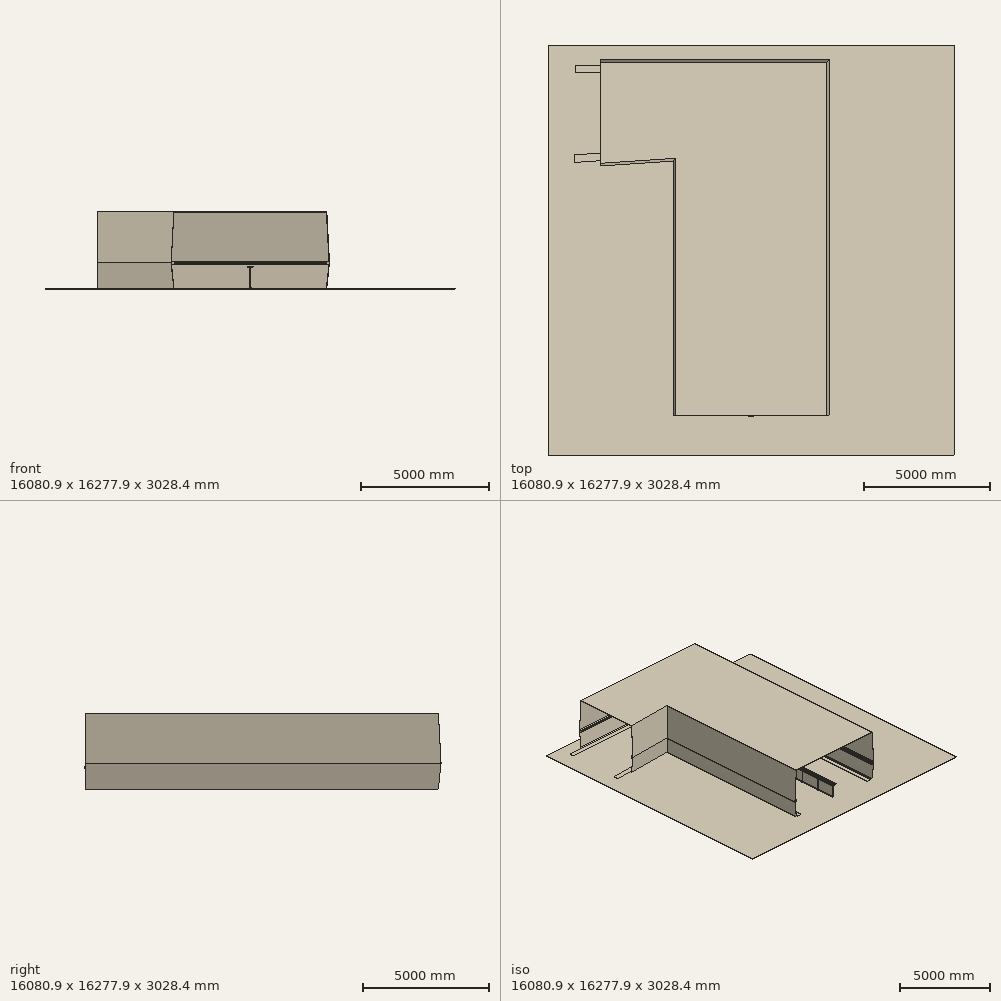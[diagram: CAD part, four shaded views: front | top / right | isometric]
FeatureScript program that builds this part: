
annotation { "Feature Type Name" : "Feature", "Feature Type Description" : "" }
export const myFeature = defineFeature(function(context is Context, id is Id, definition is map)
    precondition{}
    {
        {
            var Q0;
            Q0=qCreatedBy(makeId("Front.planeOp"),FACE);
            var sketch = newSketch(context, id + "F0", { "sketchPlane" : qUnion([Q0])});
            skLineSegment(sketch, "E0", {"start": v(-3000, -1500) * mm, "end": v(-3000, 1500) * mm, "construction": true});
            skLineSegment(sketch, "E1", {"start": v(-3000, 1500) * mm, "end": v(3000, 1500) * mm, "construction": true});
            skLineSegment(sketch, "E2", {"start": v(3000, 1500) * mm, "end": v(3000, -1500) * mm, "construction": true});
            skLineSegment(sketch, "E3.0", {"start": v(3000, 1504.6) * mm, "end": v(3000, -1500.4) * mm, "construction": true});
            skLineSegment(sketch, "E3.2", {"start": v(-3000, -1500.26) * mm, "end": v(-3000, 1504.6) * mm, "construction": true});
            skLineSegment(sketch, "E4", {"start": v(3000, 1504.6) * mm, "end": v(3104.82, -495.4) * mm});
            skLineSegment(sketch, "E5", {"start": v(3104.82, -495.4) * mm, "end": v(3000.17, -1498.75) * mm});
            skLineSegment(sketch, "E6.MirrorCS", {"start": v(-3000, 1504.6) * mm, "end": v(-3104.82, -495.4) * mm});
            skLineSegment(sketch, "E7.MirrorCS", {"start": v(-3104.82, -495.4) * mm, "end": v(-3000.17, -1498.75) * mm});
            skLineSegment(sketch, "E8", {"start": v(-3000, 1504.6) * mm, "end": v(3000, 1504.6) * mm});
            skLineSegment(sketch, "E9.0", {"start": v(3099.8, -495.26) * mm, "end": v(2995.14, -1498.75) * mm});
            skLineSegment(sketch, "E9.1", {"start": v(-3099.8, -495.26) * mm, "end": v(-2995.14, -1498.75) * mm});
            skLineSegment(sketch, "E9.2", {"start": v(-2995.26, 1499.6) * mm, "end": v(-3099.8, -495.26) * mm});
            skLineSegment(sketch, "E9.3", {"start": v(-2995.26, 1499.6) * mm, "end": v(2995.26, 1499.6) * mm});
            skLineSegment(sketch, "E9.4", {"start": v(2995.26, 1499.6) * mm, "end": v(3099.8, -495.26) * mm});
            skLineSegment(sketch, "E10", {"start": v(3000.17, -1498.75) * mm, "end": v(2995.14, -1498.75) * mm});
            skPoint(sketch, "E11.orphan", {"position": v(-3000, -1500.4) * mm});
            skLineSegment(sketch, "E12.trimOffspring", {"start": v(-2995.14, -1498.75) * mm, "end": v(-3000.17, -1498.75) * mm});
            skSolve(sketch);
        }
        {
            var Q0;
            Q0 = qSketchRegion(id + "F0", true);
            extrude(context, id + "F1", {"entities" : qUnion([Q0]), "oppositeDirection" : true, "depth" : 10000 * mm, "offsetDistance" : 25 * mm});
        }
        {
            var Q0;
            Q0=makeQuery(id+"F1.opExtrude","SWEPT_FACE",FACE,{"disambiguationData":[OSD([sQuery(id+"F0.wireOp",EDGE,"E12.trimOffspring")])]});
            var sketch = newSketch(context, id + "F2", { "sketchPlane" : qUnion([Q0])});
            skLineSegment(sketch, "E13.bottom", {"start": v(-8032.33, 1597.7) * mm, "end": v(8048.56, 1597.7) * mm});
            skLineSegment(sketch, "E13.top", {"start": v(-8032.33, -14680.18) * mm, "end": v(8048.56, -14680.18) * mm});
            skLineSegment(sketch, "E13.left", {"start": v(-8032.33, 1597.7) * mm, "end": v(-8032.33, -14680.18) * mm});
            skLineSegment(sketch, "E13.right", {"start": v(8048.56, 1597.7) * mm, "end": v(8048.56, -14680.18) * mm});
            skSolve(sketch);
        }
        {
            var Q0;
            Q0 = qSketchRegion(id + "F2", true);
            extrude(context, id + "F3", {"entities" : qUnion([Q0]), "depth" : 25 * mm, "offsetDistance" : 25 * mm});
        }
        {
            var Q0;
            Q0=makeQuery(id+"F1.opExtrude","CAP_FACE",FACE,{"disambiguationData":[OSD([sQuery(id+"F0.wireOp",EDGE,"E4"),sQuery(id+"F0.wireOp",EDGE,"E5"),sQuery(id+"F0.wireOp",EDGE,"E6.MirrorCS"),sQuery(id+"F0.wireOp",EDGE,"E7.MirrorCS"),sQuery(id+"F0.wireOp",EDGE,"E8"),sQuery(id+"F0.wireOp",EDGE,"E9.0"),sQuery(id+"F0.wireOp",EDGE,"E9.1"),sQuery(id+"F0.wireOp",EDGE,"E9.2"),sQuery(id+"F0.wireOp",EDGE,"E9.3"),sQuery(id+"F0.wireOp",EDGE,"E9.4"),sQuery(id+"F0.wireOp",EDGE,"E10"),sQuery(id+"F0.wireOp",EDGE,"E12.trimOffspring")])],"isStart":false});
            var sketch = newSketch(context, id + "F4", { "sketchPlane" : qUnion([Q0])});
            skLineSegment(sketch, "E14.0", {"start": v(-3000, 1504.6) * mm, "end": v(-3104.82, -495.4) * mm});
            skLineSegment(sketch, "E14.1", {"start": v(-2995.26, 1499.6) * mm, "end": v(-3099.8, -495.26) * mm});
            skLineSegment(sketch, "E14.2", {"start": v(-3099.8, -495.26) * mm, "end": v(-2995.14, -1498.75) * mm});
            skLineSegment(sketch, "E14.3", {"start": v(-3104.82, -495.4) * mm, "end": v(-3000.17, -1498.75) * mm});
            skLineSegment(sketch, "E14.4", {"start": v(-3000.17, -1498.75) * mm, "end": v(-2995.14, -1498.75) * mm});
            skLineSegment(sketch, "E15", {"start": v(-2995.26, 1499.6) * mm, "end": v(-2995.26, 1504.6) * mm});
            skLineSegment(sketch, "E16", {"start": v(-2995.26, 1504.6) * mm, "end": v(-3000, 1504.6) * mm});
            skSolve(sketch);
        }
        {
            var Q0;
            Q0=makeQuery(id+"F3.opExtrude","CAP_FACE",FACE,{"disambiguationData":[OSD([sQuery(id+"F2.wireOp",EDGE,"E13.bottom"),sQuery(id+"F2.wireOp",EDGE,"E13.top"),sQuery(id+"F2.wireOp",EDGE,"E13.left"),sQuery(id+"F2.wireOp",EDGE,"E13.right")])],"isStart":true});
            var sketch = newSketch(context, id + "F5", { "sketchPlane" : qUnion([Q0])});
            skLineSegment(sketch, "E17", {"start": v(3000.17, 10000) * mm, "end": v(3000.17, 14000) * mm});
            skLineSegment(sketch, "E18", {"start": v(3000.17, 14000) * mm, "end": v(-5999.83, 14000) * mm});
            skSolve(sketch);
        }
        {
            var Q0;
            Q0 = qSketchRegion(id + "F4", true);
            var Q1;
            Q1 = qConstructionFilter(qBodyType(qCreatedBy(id + "F5" ,EDGE), BodyType.WIRE), ConstructionObject.NO);
            sweep(context, id + "F6", {"operationType" : NewBodyOperationType.ADD, "profiles" : qUnion([Q0]), "path" : qUnion([Q1])});
        }
        {
            var Q0;
            Q0=makeQuery(id+"F1.opExtrude","CAP_FACE",FACE,{"disambiguationData":[OSD([sQuery(id+"F0.wireOp",EDGE,"E4"),sQuery(id+"F0.wireOp",EDGE,"E5"),sQuery(id+"F0.wireOp",EDGE,"E6.MirrorCS"),sQuery(id+"F0.wireOp",EDGE,"E7.MirrorCS"),sQuery(id+"F0.wireOp",EDGE,"E8"),sQuery(id+"F0.wireOp",EDGE,"E9.0"),sQuery(id+"F0.wireOp",EDGE,"E9.1"),sQuery(id+"F0.wireOp",EDGE,"E9.2"),sQuery(id+"F0.wireOp",EDGE,"E9.3"),sQuery(id+"F0.wireOp",EDGE,"E9.4"),sQuery(id+"F0.wireOp",EDGE,"E10"),sQuery(id+"F0.wireOp",EDGE,"E12.trimOffspring")])],"isStart":false});
            var sketch = newSketch(context, id + "F7", { "sketchPlane" : qUnion([Q0])});
            skLineSegment(sketch, "E19.0", {"start": v(3099.8, -495.26) * mm, "end": v(2995.14, -1498.75) * mm});
            skLineSegment(sketch, "E19.1", {"start": v(3104.82, -495.4) * mm, "end": v(3000.17, -1498.75) * mm});
            skLineSegment(sketch, "E19.2", {"start": v(2995.14, -1498.75) * mm, "end": v(3000.17, -1498.75) * mm});
            skLineSegment(sketch, "E19.3", {"start": v(3000, 1504.6) * mm, "end": v(3104.82, -495.4) * mm});
            skLineSegment(sketch, "E19.4", {"start": v(2995.26, 1499.6) * mm, "end": v(3099.8, -495.26) * mm});
            skLineSegment(sketch, "E20", {"start": v(2995.26, 1499.6) * mm, "end": v(2995.26, 1504.6) * mm});
            skLineSegment(sketch, "E21", {"start": v(2995.26, 1504.6) * mm, "end": v(3000, 1504.6) * mm});
            skSolve(sketch);
        }
        {
            var Q0;
            Q0=makeQuery(id+"F3.opExtrude","CAP_FACE",FACE,{"disambiguationData":[OSD([sQuery(id+"F2.wireOp",EDGE,"E13.bottom"),sQuery(id+"F2.wireOp",EDGE,"E13.top"),sQuery(id+"F2.wireOp",EDGE,"E13.left"),sQuery(id+"F2.wireOp",EDGE,"E13.right")])],"isStart":true});
            var sketch = newSketch(context, id + "F8", { "sketchPlane" : qUnion([Q0])});
            skLineSegment(sketch, "E22", {"start": v(-3000.17, 10000) * mm, "end": v(-3000.17, 10200) * mm});
            skLineSegment(sketch, "E23", {"start": v(-3000.17, 10200) * mm, "end": v(-5999.83, 10000) * mm});
            skSolve(sketch);
        }
        {
            var Q0;
            Q0 = qSketchRegion(id + "F7", true);
            var Q1;
            Q1 = qConstructionFilter(qBodyType(qCreatedBy(id + "F8" ,EDGE), BodyType.WIRE), ConstructionObject.NO);
            sweep(context, id + "F9", {"operationType" : NewBodyOperationType.ADD, "profiles" : qUnion([Q0]), "path" : qUnion([Q1])});
        }
        {
            var Q0;
            Q0=makeQuery(id+"F9.boolean.opBoolean","MERGE",FACE,{"derivedFrom":[makeQuery(id+"F6.boolean.opBoolean","MERGE",FACE,{"derivedFrom":[makeQuery(id+"F1.opExtrude","SWEPT_FACE",FACE,{"disambiguationData":[OSD([sQuery(id+"F0.wireOp",EDGE,"E8")])]}),makeQuery(id+"F6.opSweep","SWEPT_FACE",FACE,{"disambiguationData":[OSD([sQuery(id+"F4.wireOp",EDGE,"E16"),sQuery(id+"F5.wireOp",EDGE,"E17")])]})]}),makeQuery(id+"F9.opSweep","SWEPT_FACE",FACE,{"disambiguationData":[OSD([sQuery(id+"F7.wireOp",EDGE,"E21"),sQuery(id+"F8.wireOp",EDGE,"E22")])]})]});
            var sketch = newSketch(context, id + "F10", { "sketchPlane" : qUnion([Q0])});
            skLineSegment(sketch, "E24.0", {"start": v(-3000, 10200.18) * mm, "end": v(-5999.84, 10000.17) * mm});
            skLineSegment(sketch, "E24.1", {"start": v(3000, 13999.83) * mm, "end": v(-5999.83, 13999.83) * mm});
            skLineSegment(sketch, "E24.2", {"start": v(3000, 13999.83) * mm, "end": v(3000, 10000) * mm});
            skLineSegment(sketch, "E24.3", {"start": v(-2995.26, 10000) * mm, "end": v(2995.26, 10000) * mm});
            skLineSegment(sketch, "E25", {"start": v(2995.26, 10000) * mm, "end": v(3000, 10000) * mm});
            skPoint(sketch, "E26.orphan", {"position": v(3000, 0) * mm});
            skLineSegment(sketch, "E27", {"start": v(-3000, 10200.18) * mm, "end": v(-3000, 10000) * mm});
            skLineSegment(sketch, "E28", {"start": v(-3000, 10000) * mm, "end": v(-2995.26, 10000) * mm});
            skLineSegment(sketch, "E29", {"start": v(-5999.83, 13999.83) * mm, "end": v(-5999.84, 10000.17) * mm});
            skSolve(sketch);
        }
        {
            var Q0;
            Q0 = qSketchRegion(id + "F10", true);
            extrude(context, id + "F11", {"entities" : qUnion([Q0]), "operationType" : NewBodyOperationType.ADD, "oppositeDirection" : true, "depth" : 5 * mm, "offsetDistance" : 25 * mm});
        }
        {
            var Q0;
            Q0=makeQuery(id+"F1.opExtrude","CAP_FACE",FACE,{"disambiguationData":[OSD([sQuery(id+"F0.wireOp",EDGE,"E4"),sQuery(id+"F0.wireOp",EDGE,"E5"),sQuery(id+"F0.wireOp",EDGE,"E6.MirrorCS"),sQuery(id+"F0.wireOp",EDGE,"E7.MirrorCS"),sQuery(id+"F0.wireOp",EDGE,"E8"),sQuery(id+"F0.wireOp",EDGE,"E9.0"),sQuery(id+"F0.wireOp",EDGE,"E9.1"),sQuery(id+"F0.wireOp",EDGE,"E9.2"),sQuery(id+"F0.wireOp",EDGE,"E9.3"),sQuery(id+"F0.wireOp",EDGE,"E9.4"),sQuery(id+"F0.wireOp",EDGE,"E10"),sQuery(id+"F0.wireOp",EDGE,"E12.trimOffspring")])],"isStart":true});
            var sketch = newSketch(context, id + "F12", { "sketchPlane" : qUnion([Q0])});
            skLineSegment(sketch, "E30", {"start": v(3096.13, -425.26) * mm, "end": v(2976.13, -425.26) * mm});
            skLineSegment(sketch, "E31", {"start": v(2976.13, -425.26) * mm, "end": v(2976.13, -465.26) * mm});
            skLineSegment(sketch, "E32", {"start": v(2976.13, -565.26) * mm, "end": v(3016.19, -565.26) * mm});
            skLineSegment(sketch, "E33", {"start": v(3092.5, -565.26) * mm, "end": v(3099.8, -495.26) * mm});
            skLineSegment(sketch, "E34", {"start": v(3099.8, -495.26) * mm, "end": v(3096.13, -425.26) * mm});
            skLineSegment(sketch, "E35", {"start": v(2976.13, -525.26) * mm, "end": v(2986.13, -525.26) * mm});
            skLineSegment(sketch, "E36", {"start": v(2986.13, -525.26) * mm, "end": v(2986.13, -515.26) * mm});
            skLineSegment(sketch, "E37", {"start": v(2986.13, -515.26) * mm, "end": v(2976.13, -515.26) * mm});
            skLineSegment(sketch, "E38", {"start": v(2976.13, -465.26) * mm, "end": v(2986.13, -465.26) * mm});
            skLineSegment(sketch, "E39", {"start": v(2986.13, -465.26) * mm, "end": v(2986.13, -475.26) * mm});
            skLineSegment(sketch, "E40", {"start": v(2986.13, -475.26) * mm, "end": v(2976.13, -475.26) * mm});
            skLineSegment(sketch, "E41.trimOffspring", {"start": v(2976.13, -475.26) * mm, "end": v(2976.13, -515.26) * mm});
            skLineSegment(sketch, "E42.trimOffspring", {"start": v(2976.13, -525.26) * mm, "end": v(2976.13, -565.26) * mm});
            skLineSegment(sketch, "E43", {"start": v(3034.32, -565.26) * mm, "end": v(3034.32, -541.62) * mm, "construction": true});
            skLineSegment(sketch, "E44", {"start": v(3034.32, -541.62) * mm, "end": v(3024.32, -541.62) * mm});
            skLineSegment(sketch, "E45", {"start": v(3024.32, -541.62) * mm, "end": v(3016.19, -565.26) * mm});
            skLineSegment(sketch, "E46.MirrorCS", {"start": v(3044.32, -541.62) * mm, "end": v(3052.45, -565.26) * mm});
            skLineSegment(sketch, "E47.MirrorCS", {"start": v(3034.32, -541.62) * mm, "end": v(3044.32, -541.62) * mm});
            skLineSegment(sketch, "E48.trimOffspring", {"start": v(3052.45, -565.26) * mm, "end": v(3092.5, -565.26) * mm});
            skSolve(sketch);
        }
        {
            var Q0;
            Q0 = qSketchRegion(id + "F12", true);
            var Q1;
            Q1=makeQuery(id+"F6.boolean.opBoolean","MERGE",EDGE,{"derivedFrom":[makeQuery(id+"F1.opExtrude","SWEPT_EDGE",EDGE,{"disambiguationData":[OSD([sQuery(id+"F0.wireOp",EDGE,"E9.0"),sQuery(id+"F0.wireOp",EDGE,"E9.4")])]}),makeQuery(id+"F6.opSweep","SWEPT_EDGE",EDGE,{"disambiguationData":[OSD([sQuery(id+"F4.wireOp",EDGE,"E14.1"),sQuery(id+"F4.wireOp",EDGE,"E14.2"),sQuery(id+"F5.wireOp",EDGE,"E17")])]})]});
            var Q2;
            Q2=makeQuery(id+"F6.opSweep","SWEPT_EDGE",EDGE,{"disambiguationData":[OSD([sQuery(id+"F4.wireOp",EDGE,"E14.1"),sQuery(id+"F4.wireOp",EDGE,"E14.2"),sQuery(id+"F5.wireOp",EDGE,"E18")])]});
            sweep(context, id + "F13", {"profiles" : qUnion([Q0]), "path" : qUnion([Q1, Q2])});
        }
        {
            var Q0;
            {var subQ0=sQuery(id+"F0.wireOp",EDGE,"E9.4");var subQ1=sQuery(id+"F0.wireOp",EDGE,"E9.0");Q0=makeQuery(id+"F13.boolean.opBoolean","MERGE",FACE,{"derivedFrom":[makeQuery(id+"F1.opExtrude","CAP_FACE",FACE,{"disambiguationData":[OSD([sQuery(id+"F0.wireOp",EDGE,"E4"),sQuery(id+"F0.wireOp",EDGE,"E5"),sQuery(id+"F0.wireOp",EDGE,"E6.MirrorCS"),sQuery(id+"F0.wireOp",EDGE,"E7.MirrorCS"),sQuery(id+"F0.wireOp",EDGE,"E8"),subQ1,sQuery(id+"F0.wireOp",EDGE,"E9.1"),sQuery(id+"F0.wireOp",EDGE,"E9.2"),sQuery(id+"F0.wireOp",EDGE,"E9.3"),subQ0,sQuery(id+"F0.wireOp",EDGE,"E10"),sQuery(id+"F0.wireOp",EDGE,"E12.trimOffspring")])],"isStart":true}),makeQuery(id+"F13.opSweep","CAP_FACE",FACE,{"disambiguationData":[OSD([subQ1,subQ0,sQuery(id+"F12.wireOp",EDGE,"E30"),sQuery(id+"F12.wireOp",EDGE,"E31"),sQuery(id+"F12.wireOp",EDGE,"E32"),sQuery(id+"F12.wireOp",EDGE,"E33"),sQuery(id+"F12.wireOp",EDGE,"E34"),sQuery(id+"F12.wireOp",EDGE,"E35"),sQuery(id+"F12.wireOp",EDGE,"E36"),sQuery(id+"F12.wireOp",EDGE,"E37"),sQuery(id+"F12.wireOp",EDGE,"E38"),sQuery(id+"F12.wireOp",EDGE,"E39"),sQuery(id+"F12.wireOp",EDGE,"E40"),sQuery(id+"F12.wireOp",EDGE,"E41.trimOffspring"),sQuery(id+"F12.wireOp",EDGE,"E42.trimOffspring"),sQuery(id+"F12.wireOp",EDGE,"E44"),sQuery(id+"F12.wireOp",EDGE,"E45"),sQuery(id+"F12.wireOp",EDGE,"E46.MirrorCS"),sQuery(id+"F12.wireOp",EDGE,"E47.MirrorCS"),sQuery(id+"F12.wireOp",EDGE,"E48.trimOffspring")])],"isStart":true})]});}
            var sketch = newSketch(context, id + "F14", { "sketchPlane" : qUnion([Q0])});
            skLineSegment(sketch, "E49.0", {"start": v(3096.13, -425.26) * mm, "end": v(2976.13, -425.26) * mm, "construction": true});
            skLineSegment(sketch, "E49.1", {"start": v(2976.13, -425.26) * mm, "end": v(2976.13, -465.26) * mm, "construction": true});
            skLineSegment(sketch, "E49.2", {"start": v(2976.13, -565.26) * mm, "end": v(3016.19, -565.26) * mm, "construction": true});
            skLineSegment(sketch, "E49.3", {"start": v(3092.5, -565.26) * mm, "end": v(3099.8, -495.26) * mm, "construction": true});
            skLineSegment(sketch, "E49.4", {"start": v(3099.8, -495.26) * mm, "end": v(3096.13, -425.26) * mm, "construction": true});
            skLineSegment(sketch, "E49.5", {"start": v(2976.13, -525.26) * mm, "end": v(2986.13, -525.26) * mm, "construction": true});
            skLineSegment(sketch, "E49.6", {"start": v(2986.13, -525.26) * mm, "end": v(2986.13, -515.26) * mm, "construction": true});
            skLineSegment(sketch, "E49.7", {"start": v(2986.13, -515.26) * mm, "end": v(2976.13, -515.26) * mm, "construction": true});
            skLineSegment(sketch, "E49.8", {"start": v(2976.13, -465.26) * mm, "end": v(2986.13, -465.26) * mm, "construction": true});
            skLineSegment(sketch, "E49.9", {"start": v(2986.13, -465.26) * mm, "end": v(2986.13, -475.26) * mm, "construction": true});
            skLineSegment(sketch, "E49.10", {"start": v(2986.13, -475.26) * mm, "end": v(2976.13, -475.26) * mm, "construction": true});
            skLineSegment(sketch, "E49.11", {"start": v(2976.13, -475.26) * mm, "end": v(2976.13, -515.26) * mm, "construction": true});
            skLineSegment(sketch, "E49.12", {"start": v(2976.13, -525.26) * mm, "end": v(2976.13, -565.26) * mm, "construction": true});
            skLineSegment(sketch, "E49.13", {"start": v(3034.32, -565.26) * mm, "end": v(3034.32, -541.62) * mm, "construction": true});
            skLineSegment(sketch, "E49.14", {"start": v(3034.32, -541.62) * mm, "end": v(3024.32, -541.62) * mm, "construction": true});
            skLineSegment(sketch, "E49.15", {"start": v(3024.32, -541.62) * mm, "end": v(3016.19, -565.26) * mm, "construction": true});
            skLineSegment(sketch, "E49.16", {"start": v(3044.32, -541.62) * mm, "end": v(3052.45, -565.26) * mm, "construction": true});
            skLineSegment(sketch, "E49.17", {"start": v(3034.32, -541.62) * mm, "end": v(3044.32, -541.62) * mm, "construction": true});
            skLineSegment(sketch, "E49.18", {"start": v(3052.45, -565.26) * mm, "end": v(3092.5, -565.26) * mm, "construction": true});
            skLineSegment(sketch, "E50", {"start": v(3099.8, -495.26) * mm, "end": v(-3099.8, -495.26) * mm, "construction": true});
            skLineSegment(sketch, "E51", {"start": v(0, -495.26) * mm, "end": v(0, -210.15) * mm, "construction": true});
            skLineSegment(sketch, "E52.MirrorCS", {"start": v(-2976.13, -525.26) * mm, "end": v(-2976.13, -565.26) * mm});
            skLineSegment(sketch, "E53.MirrorCS", {"start": v(-2976.13, -475.26) * mm, "end": v(-2976.13, -515.26) * mm});
            skLineSegment(sketch, "E54.MirrorCS", {"start": v(-2986.13, -475.26) * mm, "end": v(-2976.13, -475.26) * mm});
            skLineSegment(sketch, "E55.MirrorCS", {"start": v(-2986.13, -465.26) * mm, "end": v(-2986.13, -475.26) * mm});
            skLineSegment(sketch, "E56.MirrorCS", {"start": v(-2976.13, -465.26) * mm, "end": v(-2986.13, -465.26) * mm});
            skLineSegment(sketch, "E57.MirrorCS", {"start": v(-2986.13, -515.26) * mm, "end": v(-2976.13, -515.26) * mm});
            skLineSegment(sketch, "E58.MirrorCS", {"start": v(-3044.32, -541.62) * mm, "end": v(-3052.45, -565.26) * mm});
            skLineSegment(sketch, "E59.MirrorCS", {"start": v(-2986.13, -525.26) * mm, "end": v(-2986.13, -515.26) * mm});
            skLineSegment(sketch, "E60.MirrorCS", {"start": v(-2976.13, -525.26) * mm, "end": v(-2986.13, -525.26) * mm});
            skLineSegment(sketch, "E61.MirrorCS", {"start": v(-3052.45, -565.26) * mm, "end": v(-3092.5, -565.26) * mm});
            skLineSegment(sketch, "E62.MirrorCS", {"start": v(-3099.8, -495.26) * mm, "end": v(-3096.13, -425.26) * mm});
            skLineSegment(sketch, "E63.MirrorCS", {"start": v(-3092.5, -565.26) * mm, "end": v(-3099.8, -495.26) * mm});
            skLineSegment(sketch, "E64.MirrorCS", {"start": v(-2976.13, -565.26) * mm, "end": v(-3016.19, -565.26) * mm});
            skLineSegment(sketch, "E65.MirrorCS", {"start": v(-2976.13, -425.26) * mm, "end": v(-2976.13, -465.26) * mm});
            skLineSegment(sketch, "E66.MirrorCS", {"start": v(-3096.13, -425.26) * mm, "end": v(-2976.13, -425.26) * mm});
            skLineSegment(sketch, "E67.MirrorCS", {"start": v(-3024.32, -541.62) * mm, "end": v(-3016.19, -565.26) * mm});
            skLineSegment(sketch, "E68.MirrorCS", {"start": v(-3034.32, -541.62) * mm, "end": v(-3024.32, -541.62) * mm});
            skLineSegment(sketch, "E69.MirrorCS", {"start": v(-3034.32, -541.62) * mm, "end": v(-3044.32, -541.62) * mm});
            skLineSegment(sketch, "E70.MirrorCS", {"start": v(-3034.32, -565.26) * mm, "end": v(-3034.32, -541.62) * mm});
            skSolve(sketch);
        }
        {
            var Q0;
            Q0 = qSketchRegion(id + "F14", true);
            var Q1;
            Q1=makeQuery(id+"F9.boolean.opBoolean","MERGE",EDGE,{"derivedFrom":[makeQuery(id+"F1.opExtrude","SWEPT_EDGE",EDGE,{"disambiguationData":[OSD([sQuery(id+"F0.wireOp",EDGE,"E9.1"),sQuery(id+"F0.wireOp",EDGE,"E9.2")])]}),makeQuery(id+"F9.opSweep","SWEPT_EDGE",EDGE,{"disambiguationData":[OSD([sQuery(id+"F7.wireOp",EDGE,"E19.0"),sQuery(id+"F7.wireOp",EDGE,"E19.4"),sQuery(id+"F8.wireOp",EDGE,"E22")])]})]});
            var Q2;
            Q2=makeQuery(id+"F9.opSweep","SWEPT_EDGE",EDGE,{"disambiguationData":[OSD([sQuery(id+"F7.wireOp",EDGE,"E19.0"),sQuery(id+"F7.wireOp",EDGE,"E19.4"),sQuery(id+"F8.wireOp",EDGE,"E23")])]});
            sweep(context, id + "F15", {"profiles" : qUnion([Q0]), "path" : qUnion([Q1, Q2])});
        }
        {
            var Q0;
            Q0=makeQuery(id+"F3.opExtrude","CAP_FACE",FACE,{"disambiguationData":[OSD([sQuery(id+"F2.wireOp",EDGE,"E13.bottom"),sQuery(id+"F2.wireOp",EDGE,"E13.top"),sQuery(id+"F2.wireOp",EDGE,"E13.left"),sQuery(id+"F2.wireOp",EDGE,"E13.right")])],"isStart":true});
            var sketch = newSketch(context, id + "F16", { "sketchPlane" : qUnion([Q0])});
            skLineSegment(sketch, "E71.0", {"start": v(-2895.14, 10312.26) * mm, "end": v(-2895.14, 0) * mm});
            skLineSegment(sketch, "E71.1", {"start": v(-2895.14, 10312.26) * mm, "end": v(-7004.33, 10038.29) * mm});
            skLineSegment(sketch, "E72.0", {"start": v(-2595.14, 10632.93) * mm, "end": v(-7016.35, 10338.15) * mm});
            skLineSegment(sketch, "E72.1", {"start": v(-2595.14, 10632.93) * mm, "end": v(-2595.14, 0) * mm});
            skLineSegment(sketch, "E73", {"start": v(-2895.14, 0) * mm, "end": v(-2595.14, 0) * mm});
            skLineSegment(sketch, "E74", {"start": v(-7016.35, 10338.15) * mm, "end": v(-7004.33, 10038.29) * mm});
            skLineSegment(sketch, "E75.0", {"start": v(2895.14, 13894.97) * mm, "end": v(2895.14, 0) * mm});
            skLineSegment(sketch, "E75.1", {"start": v(2895.14, 13894.97) * mm, "end": v(-6994.83, 13894.97) * mm});
            skLineSegment(sketch, "E76.0", {"start": v(2595.14, 13594.97) * mm, "end": v(2595.14, 0) * mm});
            skLineSegment(sketch, "E76.1", {"start": v(2595.14, 13594.97) * mm, "end": v(-6994.83, 13594.97) * mm});
            skLineSegment(sketch, "E77", {"start": v(2595.14, 0) * mm, "end": v(2895.14, 0) * mm});
            skLineSegment(sketch, "E78", {"start": v(-6994.83, 13594.97) * mm, "end": v(-6994.83, 13894.97) * mm});
            skSolve(sketch);
        }
        {
            var Q0;
            Q0 = qSketchRegion(id + "F16", true);
            extrude(context, id + "F17", {"entities" : qUnion([Q0]), "operationType" : NewBodyOperationType.REMOVE, "oppositeDirection" : true, "depth" : 25 * mm, "offsetDistance" : 25 * mm});
        }
        {
            var Q0;
            Q0=makeQuery(id+"F3.opExtrude","CAP_FACE",FACE,{"disambiguationData":[OSD([sQuery(id+"F2.wireOp",EDGE,"E13.bottom"),sQuery(id+"F2.wireOp",EDGE,"E13.top"),sQuery(id+"F2.wireOp",EDGE,"E13.left"),sQuery(id+"F2.wireOp",EDGE,"E13.right")])],"isStart":true});
            var sketch = newSketch(context, id + "F18", { "sketchPlane" : qUnion([Q0])});
            skLineSegment(sketch, "E79.0", {"start": v(-2895.14, 10312.26) * mm, "end": v(-2895.14, 0) * mm});
            skLineSegment(sketch, "E79.1", {"start": v(-2895.14, 0) * mm, "end": v(-2595.14, 0) * mm});
            skLineSegment(sketch, "E79.2", {"start": v(-2595.14, 10632.93) * mm, "end": v(-2595.14, 0) * mm});
            skLineSegment(sketch, "E79.3", {"start": v(2595.14, 13594.97) * mm, "end": v(2595.14, 0) * mm});
            skLineSegment(sketch, "E79.4", {"start": v(2595.14, 0) * mm, "end": v(2895.14, 0) * mm});
            skLineSegment(sketch, "E79.5", {"start": v(2895.14, 13894.97) * mm, "end": v(2895.14, 0) * mm});
            skLineSegment(sketch, "E79.6", {"start": v(-2595.14, 10632.93) * mm, "end": v(-7016.35, 10338.15) * mm});
            skLineSegment(sketch, "E79.7", {"start": v(-7016.35, 10338.15) * mm, "end": v(-7004.33, 10038.29) * mm});
            skLineSegment(sketch, "E79.8", {"start": v(-2895.14, 10312.26) * mm, "end": v(-7004.33, 10038.29) * mm});
            skLineSegment(sketch, "E79.9", {"start": v(2895.14, 13894.97) * mm, "end": v(-6994.83, 13894.97) * mm});
            skLineSegment(sketch, "E79.10", {"start": v(2595.14, 13594.97) * mm, "end": v(-6994.83, 13594.97) * mm});
            skLineSegment(sketch, "E79.11", {"start": v(-6994.83, 13594.97) * mm, "end": v(-6994.83, 13894.97) * mm});
            skPoint(sketch, "E79.12", {"position": v(2745.14, 0) * mm});
            skSolve(sketch);
        }
        {
            var Q0;
            Q0 = qSketchRegion(id + "F18", true);
            var Q1;
            Q1=makeQuery(id+"F3.opExtrude","CAP_FACE",FACE,{"disambiguationData":[OSD([sQuery(id+"F2.wireOp",EDGE,"E13.bottom"),sQuery(id+"F2.wireOp",EDGE,"E13.top"),sQuery(id+"F2.wireOp",EDGE,"E13.left"),sQuery(id+"F2.wireOp",EDGE,"E13.right")])],"isStart":false});
            extrude(context, id + "F19", {"entities" : qUnion([Q0]), "endBound" : BoundingType.UP_TO_SURFACE, "oppositeDirection" : true, "depth" : 25 * mm, "endBoundEntityFace" : qUnion([Q1]), "offsetDistance" : 25 * mm});
        }
        {
            var Q0;
            Q0=makeQuery(id+"F13.opSweep","MID_CAP_EDGE",EDGE,{"disambiguationData":[OSD([sQuery(id+"F4.wireOp",EDGE,"E14.1"),sQuery(id+"F4.wireOp",EDGE,"E14.2"),sQuery(id+"F5.wireOp",EDGE,"E17"),sQuery(id+"F12.wireOp",EDGE,"E31")])],"capPos":1.0});
            var Q1;
            Q1=makeQuery(id+"F13.opSweep","MID_CAP_EDGE",EDGE,{"disambiguationData":[OSD([sQuery(id+"F4.wireOp",EDGE,"E14.1"),sQuery(id+"F4.wireOp",EDGE,"E14.2"),sQuery(id+"F5.wireOp",EDGE,"E17"),sQuery(id+"F12.wireOp",EDGE,"E42.trimOffspring")])],"capPos":1.0});
            var Q2;
            Q2=makeQuery(id+"F13.opSweep","MID_CAP_EDGE",EDGE,{"disambiguationData":[OSD([sQuery(id+"F4.wireOp",EDGE,"E14.1"),sQuery(id+"F4.wireOp",EDGE,"E14.2"),sQuery(id+"F5.wireOp",EDGE,"E17"),sQuery(id+"F12.wireOp",EDGE,"E41.trimOffspring")])],"capPos":1.0});
            var Q3;
            Q3=makeQuery(id+"F15.opSweep","MID_CAP_EDGE",EDGE,{"disambiguationData":[OSD([sQuery(id+"F7.wireOp",EDGE,"E19.0"),sQuery(id+"F7.wireOp",EDGE,"E19.4"),sQuery(id+"F8.wireOp",EDGE,"E22"),sQuery(id+"F14.wireOp",EDGE,"E65.MirrorCS")])],"capPos":1.0});
            var Q4;
            Q4=makeQuery(id+"F15.opSweep","MID_CAP_EDGE",EDGE,{"disambiguationData":[OSD([sQuery(id+"F7.wireOp",EDGE,"E19.0"),sQuery(id+"F7.wireOp",EDGE,"E19.4"),sQuery(id+"F8.wireOp",EDGE,"E22"),sQuery(id+"F14.wireOp",EDGE,"E53.MirrorCS")])],"capPos":1.0});
            var Q5;
            Q5=makeQuery(id+"F15.opSweep","MID_CAP_EDGE",EDGE,{"disambiguationData":[OSD([sQuery(id+"F7.wireOp",EDGE,"E19.0"),sQuery(id+"F7.wireOp",EDGE,"E19.4"),sQuery(id+"F8.wireOp",EDGE,"E22"),sQuery(id+"F14.wireOp",EDGE,"E52.MirrorCS")])],"capPos":1.0});
            var Q6;
            Q6=makeQuery(id+"F15.opSweep","MID_CAP_EDGE",EDGE,{"disambiguationData":[OSD([sQuery(id+"F7.wireOp",EDGE,"E19.0"),sQuery(id+"F7.wireOp",EDGE,"E19.4"),sQuery(id+"F8.wireOp",EDGE,"E22"),sQuery(id+"F14.wireOp",EDGE,"E55.MirrorCS")])],"capPos":1.0});
            var Q7;
            Q7=makeQuery(id+"F15.opSweep","MID_CAP_EDGE",EDGE,{"disambiguationData":[OSD([sQuery(id+"F7.wireOp",EDGE,"E19.0"),sQuery(id+"F7.wireOp",EDGE,"E19.4"),sQuery(id+"F8.wireOp",EDGE,"E22"),sQuery(id+"F14.wireOp",EDGE,"E59.MirrorCS")])],"capPos":1.0});
            fillet(context, id + "F20", {"entities" : qUnion([Q0, Q1, Q2, Q3, Q4, Q5, Q6, Q7]), "radius" : 5 * mm, "tangentPropagation" : true, "allowEdgeOverflow" : false});
        }
        {
            var Q0;
            Q0=makeQuery(id+"F13.opSweep","SWEPT_EDGE",EDGE,{"disambiguationData":[OSD([sQuery(id+"F0.wireOp",EDGE,"E9.0"),sQuery(id+"F0.wireOp",EDGE,"E9.4"),sQuery(id+"F4.wireOp",EDGE,"E14.1"),sQuery(id+"F4.wireOp",EDGE,"E14.2"),sQuery(id+"F5.wireOp",EDGE,"E17"),sQuery(id+"F12.wireOp",EDGE,"E30"),sQuery(id+"F12.wireOp",EDGE,"E31")])]});
            var Q1;
            Q1=makeQuery(id+"F13.opSweep","SWEPT_EDGE",EDGE,{"disambiguationData":[OSD([sQuery(id+"F0.wireOp",EDGE,"E9.0"),sQuery(id+"F0.wireOp",EDGE,"E9.4"),sQuery(id+"F4.wireOp",EDGE,"E14.1"),sQuery(id+"F4.wireOp",EDGE,"E14.2"),sQuery(id+"F5.wireOp",EDGE,"E17"),sQuery(id+"F12.wireOp",EDGE,"E32"),sQuery(id+"F12.wireOp",EDGE,"E42.trimOffspring")])]});
            var Q2;
            Q2=makeQuery(id+"F15.opSweep","SWEPT_EDGE",EDGE,{"disambiguationData":[OSD([sQuery(id+"F0.wireOp",EDGE,"E9.1"),sQuery(id+"F0.wireOp",EDGE,"E9.2"),sQuery(id+"F7.wireOp",EDGE,"E19.0"),sQuery(id+"F7.wireOp",EDGE,"E19.4"),sQuery(id+"F8.wireOp",EDGE,"E22"),sQuery(id+"F14.wireOp",EDGE,"E65.MirrorCS"),sQuery(id+"F14.wireOp",EDGE,"E66.MirrorCS")])]});
            var Q3;
            Q3=makeQuery(id+"F15.opSweep","SWEPT_EDGE",EDGE,{"disambiguationData":[OSD([sQuery(id+"F0.wireOp",EDGE,"E9.1"),sQuery(id+"F0.wireOp",EDGE,"E9.2"),sQuery(id+"F7.wireOp",EDGE,"E19.0"),sQuery(id+"F7.wireOp",EDGE,"E19.4"),sQuery(id+"F8.wireOp",EDGE,"E22"),sQuery(id+"F14.wireOp",EDGE,"E52.MirrorCS"),sQuery(id+"F14.wireOp",EDGE,"E64.MirrorCS")])]});
            fillet(context, id + "F21", {"entities" : qUnion([Q0, Q1, Q2, Q3]), "radius" : 10 * mm, "tangentPropagation" : true, "allowEdgeOverflow" : false});
        }
        {
            var Q0;
            Q0=makeQuery(id+"F15.opSweep","SWEPT_EDGE",EDGE,{"disambiguationData":[OSD([sQuery(id+"F7.wireOp",EDGE,"E19.0"),sQuery(id+"F7.wireOp",EDGE,"E19.4"),sQuery(id+"F8.wireOp",EDGE,"E23"),sQuery(id+"F14.wireOp",EDGE,"E56.MirrorCS"),sQuery(id+"F14.wireOp",EDGE,"E65.MirrorCS")])]});
            var Q1;
            Q1=makeQuery(id+"F15.opSweep","SWEPT_EDGE",EDGE,{"disambiguationData":[OSD([sQuery(id+"F7.wireOp",EDGE,"E19.0"),sQuery(id+"F7.wireOp",EDGE,"E19.4"),sQuery(id+"F8.wireOp",EDGE,"E23"),sQuery(id+"F14.wireOp",EDGE,"E53.MirrorCS"),sQuery(id+"F14.wireOp",EDGE,"E54.MirrorCS")])]});
            var Q2;
            Q2=makeQuery(id+"F15.opSweep","SWEPT_EDGE",EDGE,{"disambiguationData":[OSD([sQuery(id+"F7.wireOp",EDGE,"E19.0"),sQuery(id+"F7.wireOp",EDGE,"E19.4"),sQuery(id+"F8.wireOp",EDGE,"E23"),sQuery(id+"F14.wireOp",EDGE,"E53.MirrorCS"),sQuery(id+"F14.wireOp",EDGE,"E57.MirrorCS")])]});
            var Q3;
            Q3=makeQuery(id+"F15.opSweep","SWEPT_EDGE",EDGE,{"disambiguationData":[OSD([sQuery(id+"F7.wireOp",EDGE,"E19.0"),sQuery(id+"F7.wireOp",EDGE,"E19.4"),sQuery(id+"F8.wireOp",EDGE,"E23"),sQuery(id+"F14.wireOp",EDGE,"E52.MirrorCS"),sQuery(id+"F14.wireOp",EDGE,"E60.MirrorCS")])]});
            var Q4;
            Q4=makeQuery(id+"F13.opSweep","SWEPT_EDGE",EDGE,{"disambiguationData":[OSD([sQuery(id+"F0.wireOp",EDGE,"E9.0"),sQuery(id+"F0.wireOp",EDGE,"E9.4"),sQuery(id+"F4.wireOp",EDGE,"E14.1"),sQuery(id+"F4.wireOp",EDGE,"E14.2"),sQuery(id+"F5.wireOp",EDGE,"E17"),sQuery(id+"F12.wireOp",EDGE,"E35"),sQuery(id+"F12.wireOp",EDGE,"E42.trimOffspring")])]});
            var Q5;
            Q5=makeQuery(id+"F13.opSweep","SWEPT_EDGE",EDGE,{"disambiguationData":[OSD([sQuery(id+"F0.wireOp",EDGE,"E9.0"),sQuery(id+"F0.wireOp",EDGE,"E9.4"),sQuery(id+"F4.wireOp",EDGE,"E14.1"),sQuery(id+"F4.wireOp",EDGE,"E14.2"),sQuery(id+"F5.wireOp",EDGE,"E17"),sQuery(id+"F12.wireOp",EDGE,"E37"),sQuery(id+"F12.wireOp",EDGE,"E41.trimOffspring")])]});
            var Q6;
            Q6=makeQuery(id+"F13.opSweep","SWEPT_EDGE",EDGE,{"disambiguationData":[OSD([sQuery(id+"F0.wireOp",EDGE,"E9.0"),sQuery(id+"F0.wireOp",EDGE,"E9.4"),sQuery(id+"F4.wireOp",EDGE,"E14.1"),sQuery(id+"F4.wireOp",EDGE,"E14.2"),sQuery(id+"F5.wireOp",EDGE,"E17"),sQuery(id+"F12.wireOp",EDGE,"E40"),sQuery(id+"F12.wireOp",EDGE,"E41.trimOffspring")])]});
            var Q7;
            Q7=makeQuery(id+"F13.opSweep","SWEPT_EDGE",EDGE,{"disambiguationData":[OSD([sQuery(id+"F0.wireOp",EDGE,"E9.0"),sQuery(id+"F0.wireOp",EDGE,"E9.4"),sQuery(id+"F4.wireOp",EDGE,"E14.1"),sQuery(id+"F4.wireOp",EDGE,"E14.2"),sQuery(id+"F5.wireOp",EDGE,"E17"),sQuery(id+"F12.wireOp",EDGE,"E31"),sQuery(id+"F12.wireOp",EDGE,"E38")])]});
            fillet(context, id + "F22", {"entities" : qUnion([Q0, Q1, Q2, Q3, Q4, Q5, Q6, Q7]), "radius" : 5 * mm, "tangentPropagation" : true, "allowEdgeOverflow" : false});
        }
        {
            var Q0;
            Q0=makeQuery(id+"F3.opExtrude","CAP_FACE",FACE,{"disambiguationData":[OSD([sQuery(id+"F2.wireOp",EDGE,"E13.bottom"),sQuery(id+"F2.wireOp",EDGE,"E13.top"),sQuery(id+"F2.wireOp",EDGE,"E13.left"),sQuery(id+"F2.wireOp",EDGE,"E13.right")])],"isStart":true});
            var sketch = newSketch(context, id + "F23", { "sketchPlane" : qUnion([Q0])});
            skLineSegment(sketch, "E80", {"start": v(-2595.14, 0) * mm, "end": v(2595.14, 0) * mm, "construction": true});
            skLineSegment(sketch, "E81", {"start": v(0, 0) * mm, "end": v(0, 10632.93) * mm, "construction": true});
            skCircle(sketch, "E82", {"center": v(0, 100) * mm, "radius": 40 * mm});
            skCircle(sketch, "E83.0.1.0", {"center": v(0, 1300) * mm, "radius": 40 * mm});
            skCircle(sketch, "E83.0.2.0", {"center": v(0, 2500) * mm, "radius": 40 * mm});
            skCircle(sketch, "E83.0.3.0", {"center": v(0, 3700) * mm, "radius": 40 * mm});
            skCircle(sketch, "E83.0.4.0", {"center": v(0, 4900) * mm, "radius": 40 * mm});
            skCircle(sketch, "E83.0.5.0", {"center": v(0, 6100) * mm, "radius": 40 * mm});
            skCircle(sketch, "E83.0.6.0", {"center": v(0, 7300) * mm, "radius": 40 * mm});
            skCircle(sketch, "E83.0.7.0", {"center": v(0, 8500) * mm, "radius": 40 * mm});
            skCircle(sketch, "E83.0.8.0", {"center": v(0, 9700) * mm, "radius": 40 * mm});
            skLineSegment(sketch, "E83.direction1", {"start": v(0, 100) * mm, "end": v(0, 100) * mm});
            skLineSegment(sketch, "E83.direction2", {"start": v(0, 100) * mm, "end": v(0, 1300) * mm, "construction": true});
            skSolve(sketch);
        }
        {
            var Q0;
            Q0 = qSketchRegion(id + "F23", true);
            extrude(context, id + "F24", {"entities" : qUnion([Q0]), "depth" : 25 * mm, "offsetDistance" : 25 * mm});
        }
        {
            var Q0;
            Q0=makeQuery(id+"F24.opExtrude","CAP_FACE",FACE,{"disambiguationData":[OSD([sQuery(id+"F23.wireOp",EDGE,"E82")])],"isStart":false});
            var sketch = newSketch(context, id + "F25", { "sketchPlane" : qUnion([Q0])});
            skArc(sketch, "E84", {"start": v(-6, 129.4) * mm, "mid": v(-11.18, 127.84) * mm, "end": v(-16, 125.38) * mm});
            skLineSegment(sketch, "E85", {"start": v(0, 100) * mm, "end": v(0, 130) * mm, "construction": true});
            skLineSegment(sketch, "E86.0", {"start": v(6, 100) * mm, "end": v(6, 129.4) * mm});
            skLineSegment(sketch, "E87.0", {"start": v(-6, 100) * mm, "end": v(-6, 129.4) * mm});
            skLineSegment(sketch, "E88", {"start": v(-6, 100) * mm, "end": v(6, 100) * mm});
            skCircle(sketch, "E89.0", {"center": v(0, 1300) * mm, "radius": 40 * mm, "construction": true});
            skArc(sketch, "E90", {"start": v(6, 1270.6) * mm, "mid": v(11.18, 1272.16) * mm, "end": v(16, 1274.62) * mm});
            skLineSegment(sketch, "E91.0", {"start": v(-6, 1292) * mm, "end": v(-6, 1270.6) * mm});
            skLineSegment(sketch, "E92.0", {"start": v(6, 1292) * mm, "end": v(6, 1270.6) * mm});
            skLineSegment(sketch, "E93", {"start": v(-6, 1292) * mm, "end": v(6, 1292) * mm});
            skPoint(sketch, "E93.endSnap0", {"position": v(6, 1285) * mm});
            skPoint(sketch, "E94.orphan", {"position": v(6, 1300) * mm});
            skPoint(sketch, "E95.orphan", {"position": v(6, 1270) * mm});
            skLineSegment(sketch, "E96", {"start": v(-20.78, 1300) * mm, "end": v(22.57, 1300) * mm, "construction": true});
            skLineSegment(sketch, "E97.MirrorCS", {"start": v(6, 1308) * mm, "end": v(6, 1329.4) * mm});
            skPoint(sketch, "E98.MirrorP", {"position": v(6, 1330) * mm});
            skPoint(sketch, "E99.MirrorP", {"position": v(6, 1315) * mm});
            skLineSegment(sketch, "E100.MirrorCS", {"start": v(-6, 1308) * mm, "end": v(6, 1308) * mm});
            skLineSegment(sketch, "E101.MirrorCS", {"start": v(-6, 1308) * mm, "end": v(-6, 1329.4) * mm});
            skArc(sketch, "E102.trimOffspring", {"start": v(-6, 1329.4) * mm, "mid": v(-11.18, 1327.84) * mm, "end": v(-16, 1325.38) * mm});
            skLineSegment(sketch, "E103.direction1", {"start": v(-6, 1270.6) * mm, "end": v(19, 1270.6) * mm, "construction": true});
            skLineSegment(sketch, "E104", {"start": v(-16, 1274.62) * mm, "end": v(-16, 1325.38) * mm});
            skLineSegment(sketch, "E105", {"start": v(16, 1274.62) * mm, "end": v(16, 1325.38) * mm});
            skArc(sketch, "E106.trimOffspring", {"start": v(-16, 1274.62) * mm, "mid": v(-11.18, 1272.16) * mm, "end": v(-6, 1270.6) * mm});
            skArc(sketch, "E107.trimOffspring", {"start": v(16, 1325.38) * mm, "mid": v(11.18, 1327.84) * mm, "end": v(6, 1329.4) * mm});
            skLineSegment(sketch, "E108", {"start": v(-16, 125.38) * mm, "end": v(-16, 74.62) * mm});
            skLineSegment(sketch, "E109", {"start": v(16, 125.38) * mm, "end": v(16, 74.62) * mm});
            skArc(sketch, "E110.trimOffspring", {"start": v(-16, 74.62) * mm, "mid": v(0, 70) * mm, "end": v(16, 74.62) * mm});
            skArc(sketch, "E111.trimOffspring", {"start": v(16, 125.38) * mm, "mid": v(11.18, 127.84) * mm, "end": v(6, 129.4) * mm});
            skCircle(sketch, "E112.0.1.0", {"center": v(0, 2500) * mm, "radius": 40 * mm, "construction": true});
            skPoint(sketch, "E112.0.1.1", {"position": v(6, 2530) * mm});
            skPoint(sketch, "E112.0.1.2", {"position": v(6, 2470) * mm});
            skPoint(sketch, "E112.0.1.3", {"position": v(6, 2485) * mm});
            skPoint(sketch, "E112.0.1.4", {"position": v(6, 2500) * mm});
            skPoint(sketch, "E112.0.1.5", {"position": v(6, 2515) * mm});
            skLineSegment(sketch, "E112.0.1.6", {"start": v(-16, 2474.62) * mm, "end": v(-16, 2525.38) * mm});
            skArc(sketch, "E112.0.1.7", {"start": v(-16, 2474.62) * mm, "mid": v(-11.18, 2472.16) * mm, "end": v(-6, 2470.6) * mm});
            skLineSegment(sketch, "E112.0.1.8", {"start": v(-6, 2470.6) * mm, "end": v(19, 2470.6) * mm, "construction": true});
            skArc(sketch, "E112.0.1.9", {"start": v(-6, 2529.4) * mm, "mid": v(-11.18, 2527.84) * mm, "end": v(-16, 2525.38) * mm});
            skLineSegment(sketch, "E112.0.1.10", {"start": v(-6, 2508) * mm, "end": v(-6, 2529.4) * mm});
            skLineSegment(sketch, "E112.0.1.11", {"start": v(-20.78, 2500) * mm, "end": v(22.57, 2500) * mm, "construction": true});
            skLineSegment(sketch, "E112.0.1.12", {"start": v(6, 2508) * mm, "end": v(6, 2529.4) * mm});
            skLineSegment(sketch, "E112.0.1.13", {"start": v(-6, 2492) * mm, "end": v(-6, 2470.6) * mm});
            skLineSegment(sketch, "E112.0.1.14", {"start": v(6, 2492) * mm, "end": v(6, 2470.6) * mm});
            skArc(sketch, "E112.0.1.15", {"start": v(16, 2525.38) * mm, "mid": v(11.18, 2527.84) * mm, "end": v(6, 2529.4) * mm});
            skArc(sketch, "E112.0.1.16", {"start": v(6, 2470.6) * mm, "mid": v(11.18, 2472.16) * mm, "end": v(16, 2474.62) * mm});
            skLineSegment(sketch, "E112.0.1.17", {"start": v(16, 2474.62) * mm, "end": v(16, 2525.38) * mm});
            skLineSegment(sketch, "E112.0.1.18", {"start": v(-6, 2508) * mm, "end": v(6, 2508) * mm});
            skLineSegment(sketch, "E112.0.1.19", {"start": v(-6, 2492) * mm, "end": v(6, 2492) * mm});
            skCircle(sketch, "E112.0.2.0", {"center": v(0, 3700) * mm, "radius": 40 * mm, "construction": true});
            skPoint(sketch, "E112.0.2.1", {"position": v(6, 3730) * mm});
            skPoint(sketch, "E112.0.2.2", {"position": v(6, 3670) * mm});
            skPoint(sketch, "E112.0.2.3", {"position": v(6, 3685) * mm});
            skPoint(sketch, "E112.0.2.4", {"position": v(6, 3700) * mm});
            skPoint(sketch, "E112.0.2.5", {"position": v(6, 3715) * mm});
            skLineSegment(sketch, "E112.0.2.6", {"start": v(-16, 3674.62) * mm, "end": v(-16, 3725.38) * mm});
            skArc(sketch, "E112.0.2.7", {"start": v(-16, 3674.62) * mm, "mid": v(-11.18, 3672.16) * mm, "end": v(-6, 3670.6) * mm});
            skLineSegment(sketch, "E112.0.2.8", {"start": v(-6, 3670.6) * mm, "end": v(19, 3670.6) * mm, "construction": true});
            skArc(sketch, "E112.0.2.9", {"start": v(-6, 3729.4) * mm, "mid": v(-11.18, 3727.84) * mm, "end": v(-16, 3725.38) * mm});
            skLineSegment(sketch, "E112.0.2.10", {"start": v(-6, 3708) * mm, "end": v(-6, 3729.4) * mm});
            skLineSegment(sketch, "E112.0.2.11", {"start": v(-20.78, 3700) * mm, "end": v(22.57, 3700) * mm, "construction": true});
            skLineSegment(sketch, "E112.0.2.12", {"start": v(6, 3708) * mm, "end": v(6, 3729.4) * mm});
            skLineSegment(sketch, "E112.0.2.13", {"start": v(-6, 3692) * mm, "end": v(-6, 3670.6) * mm});
            skLineSegment(sketch, "E112.0.2.14", {"start": v(6, 3692) * mm, "end": v(6, 3670.6) * mm});
            skArc(sketch, "E112.0.2.15", {"start": v(16, 3725.38) * mm, "mid": v(11.18, 3727.84) * mm, "end": v(6, 3729.4) * mm});
            skArc(sketch, "E112.0.2.16", {"start": v(6, 3670.6) * mm, "mid": v(11.18, 3672.16) * mm, "end": v(16, 3674.62) * mm});
            skLineSegment(sketch, "E112.0.2.17", {"start": v(16, 3674.62) * mm, "end": v(16, 3725.38) * mm});
            skLineSegment(sketch, "E112.0.2.18", {"start": v(-6, 3708) * mm, "end": v(6, 3708) * mm});
            skLineSegment(sketch, "E112.0.2.19", {"start": v(-6, 3692) * mm, "end": v(6, 3692) * mm});
            skCircle(sketch, "E112.0.3.0", {"center": v(0, 4900) * mm, "radius": 40 * mm, "construction": true});
            skPoint(sketch, "E112.0.3.1", {"position": v(6, 4930) * mm});
            skPoint(sketch, "E112.0.3.2", {"position": v(6, 4870) * mm});
            skPoint(sketch, "E112.0.3.3", {"position": v(6, 4885) * mm});
            skPoint(sketch, "E112.0.3.4", {"position": v(6, 4900) * mm});
            skPoint(sketch, "E112.0.3.5", {"position": v(6, 4915) * mm});
            skLineSegment(sketch, "E112.0.3.6", {"start": v(-16, 4874.62) * mm, "end": v(-16, 4925.38) * mm});
            skArc(sketch, "E112.0.3.7", {"start": v(-16, 4874.62) * mm, "mid": v(-11.18, 4872.16) * mm, "end": v(-6, 4870.6) * mm});
            skLineSegment(sketch, "E112.0.3.8", {"start": v(-6, 4870.6) * mm, "end": v(19, 4870.6) * mm, "construction": true});
            skArc(sketch, "E112.0.3.9", {"start": v(-6, 4929.4) * mm, "mid": v(-11.18, 4927.84) * mm, "end": v(-16, 4925.38) * mm});
            skLineSegment(sketch, "E112.0.3.10", {"start": v(-6, 4908) * mm, "end": v(-6, 4929.4) * mm});
            skLineSegment(sketch, "E112.0.3.11", {"start": v(-20.78, 4900) * mm, "end": v(22.57, 4900) * mm, "construction": true});
            skLineSegment(sketch, "E112.0.3.12", {"start": v(6, 4908) * mm, "end": v(6, 4929.4) * mm});
            skLineSegment(sketch, "E112.0.3.13", {"start": v(-6, 4892) * mm, "end": v(-6, 4870.6) * mm});
            skLineSegment(sketch, "E112.0.3.14", {"start": v(6, 4892) * mm, "end": v(6, 4870.6) * mm});
            skArc(sketch, "E112.0.3.15", {"start": v(16, 4925.38) * mm, "mid": v(11.18, 4927.84) * mm, "end": v(6, 4929.4) * mm});
            skArc(sketch, "E112.0.3.16", {"start": v(6, 4870.6) * mm, "mid": v(11.18, 4872.16) * mm, "end": v(16, 4874.62) * mm});
            skLineSegment(sketch, "E112.0.3.17", {"start": v(16, 4874.62) * mm, "end": v(16, 4925.38) * mm});
            skLineSegment(sketch, "E112.0.3.18", {"start": v(-6, 4908) * mm, "end": v(6, 4908) * mm});
            skLineSegment(sketch, "E112.0.3.19", {"start": v(-6, 4892) * mm, "end": v(6, 4892) * mm});
            skCircle(sketch, "E112.0.4.0", {"center": v(0, 6100) * mm, "radius": 40 * mm, "construction": true});
            skPoint(sketch, "E112.0.4.1", {"position": v(6, 6130) * mm});
            skPoint(sketch, "E112.0.4.2", {"position": v(6, 6070) * mm});
            skPoint(sketch, "E112.0.4.3", {"position": v(6, 6085) * mm});
            skPoint(sketch, "E112.0.4.4", {"position": v(6, 6100) * mm});
            skPoint(sketch, "E112.0.4.5", {"position": v(6, 6115) * mm});
            skLineSegment(sketch, "E112.0.4.6", {"start": v(-16, 6074.62) * mm, "end": v(-16, 6125.38) * mm});
            skArc(sketch, "E112.0.4.7", {"start": v(-16, 6074.62) * mm, "mid": v(-11.18, 6072.16) * mm, "end": v(-6, 6070.6) * mm});
            skLineSegment(sketch, "E112.0.4.8", {"start": v(-6, 6070.6) * mm, "end": v(19, 6070.6) * mm, "construction": true});
            skArc(sketch, "E112.0.4.9", {"start": v(-6, 6129.4) * mm, "mid": v(-11.18, 6127.84) * mm, "end": v(-16, 6125.38) * mm});
            skLineSegment(sketch, "E112.0.4.10", {"start": v(-6, 6108) * mm, "end": v(-6, 6129.4) * mm});
            skLineSegment(sketch, "E112.0.4.11", {"start": v(-20.78, 6100) * mm, "end": v(22.57, 6100) * mm, "construction": true});
            skLineSegment(sketch, "E112.0.4.12", {"start": v(6, 6108) * mm, "end": v(6, 6129.4) * mm});
            skLineSegment(sketch, "E112.0.4.13", {"start": v(-6, 6092) * mm, "end": v(-6, 6070.6) * mm});
            skLineSegment(sketch, "E112.0.4.14", {"start": v(6, 6092) * mm, "end": v(6, 6070.6) * mm});
            skArc(sketch, "E112.0.4.15", {"start": v(16, 6125.38) * mm, "mid": v(11.18, 6127.84) * mm, "end": v(6, 6129.4) * mm});
            skArc(sketch, "E112.0.4.16", {"start": v(6, 6070.6) * mm, "mid": v(11.18, 6072.16) * mm, "end": v(16, 6074.62) * mm});
            skLineSegment(sketch, "E112.0.4.17", {"start": v(16, 6074.62) * mm, "end": v(16, 6125.38) * mm});
            skLineSegment(sketch, "E112.0.4.18", {"start": v(-6, 6108) * mm, "end": v(6, 6108) * mm});
            skLineSegment(sketch, "E112.0.4.19", {"start": v(-6, 6092) * mm, "end": v(6, 6092) * mm});
            skCircle(sketch, "E112.0.5.0", {"center": v(0, 7300) * mm, "radius": 40 * mm, "construction": true});
            skPoint(sketch, "E112.0.5.1", {"position": v(6, 7330) * mm});
            skPoint(sketch, "E112.0.5.2", {"position": v(6, 7270) * mm});
            skPoint(sketch, "E112.0.5.3", {"position": v(6, 7285) * mm});
            skPoint(sketch, "E112.0.5.4", {"position": v(6, 7300) * mm});
            skPoint(sketch, "E112.0.5.5", {"position": v(6, 7315) * mm});
            skLineSegment(sketch, "E112.0.5.6", {"start": v(-16, 7274.62) * mm, "end": v(-16, 7325.38) * mm});
            skArc(sketch, "E112.0.5.7", {"start": v(-16, 7274.62) * mm, "mid": v(-11.18, 7272.16) * mm, "end": v(-6, 7270.6) * mm});
            skLineSegment(sketch, "E112.0.5.8", {"start": v(-6, 7270.6) * mm, "end": v(19, 7270.6) * mm, "construction": true});
            skArc(sketch, "E112.0.5.9", {"start": v(-6, 7329.4) * mm, "mid": v(-11.18, 7327.84) * mm, "end": v(-16, 7325.38) * mm});
            skLineSegment(sketch, "E112.0.5.10", {"start": v(-6, 7308) * mm, "end": v(-6, 7329.4) * mm});
            skLineSegment(sketch, "E112.0.5.11", {"start": v(-20.78, 7300) * mm, "end": v(22.57, 7300) * mm, "construction": true});
            skLineSegment(sketch, "E112.0.5.12", {"start": v(6, 7308) * mm, "end": v(6, 7329.4) * mm});
            skLineSegment(sketch, "E112.0.5.13", {"start": v(-6, 7292) * mm, "end": v(-6, 7270.6) * mm});
            skLineSegment(sketch, "E112.0.5.14", {"start": v(6, 7292) * mm, "end": v(6, 7270.6) * mm});
            skArc(sketch, "E112.0.5.15", {"start": v(16, 7325.38) * mm, "mid": v(11.18, 7327.84) * mm, "end": v(6, 7329.4) * mm});
            skArc(sketch, "E112.0.5.16", {"start": v(6, 7270.6) * mm, "mid": v(11.18, 7272.16) * mm, "end": v(16, 7274.62) * mm});
            skLineSegment(sketch, "E112.0.5.17", {"start": v(16, 7274.62) * mm, "end": v(16, 7325.38) * mm});
            skLineSegment(sketch, "E112.0.5.18", {"start": v(-6, 7308) * mm, "end": v(6, 7308) * mm});
            skLineSegment(sketch, "E112.0.5.19", {"start": v(-6, 7292) * mm, "end": v(6, 7292) * mm});
            skCircle(sketch, "E112.0.6.0", {"center": v(0, 8500) * mm, "radius": 40 * mm, "construction": true});
            skPoint(sketch, "E112.0.6.1", {"position": v(6, 8530) * mm});
            skPoint(sketch, "E112.0.6.2", {"position": v(6, 8470) * mm});
            skPoint(sketch, "E112.0.6.3", {"position": v(6, 8485) * mm});
            skPoint(sketch, "E112.0.6.4", {"position": v(6, 8500) * mm});
            skPoint(sketch, "E112.0.6.5", {"position": v(6, 8515) * mm});
            skLineSegment(sketch, "E112.0.6.6", {"start": v(-16, 8474.62) * mm, "end": v(-16, 8525.38) * mm});
            skArc(sketch, "E112.0.6.7", {"start": v(-16, 8474.62) * mm, "mid": v(-11.18, 8472.16) * mm, "end": v(-6, 8470.6) * mm});
            skLineSegment(sketch, "E112.0.6.8", {"start": v(-6, 8470.6) * mm, "end": v(19, 8470.6) * mm, "construction": true});
            skArc(sketch, "E112.0.6.9", {"start": v(-6, 8529.4) * mm, "mid": v(-11.18, 8527.84) * mm, "end": v(-16, 8525.38) * mm});
            skLineSegment(sketch, "E112.0.6.10", {"start": v(-6, 8508) * mm, "end": v(-6, 8529.4) * mm});
            skLineSegment(sketch, "E112.0.6.11", {"start": v(-20.78, 8500) * mm, "end": v(22.57, 8500) * mm, "construction": true});
            skLineSegment(sketch, "E112.0.6.12", {"start": v(6, 8508) * mm, "end": v(6, 8529.4) * mm});
            skLineSegment(sketch, "E112.0.6.13", {"start": v(-6, 8492) * mm, "end": v(-6, 8470.6) * mm});
            skLineSegment(sketch, "E112.0.6.14", {"start": v(6, 8492) * mm, "end": v(6, 8470.6) * mm});
            skArc(sketch, "E112.0.6.15", {"start": v(16, 8525.38) * mm, "mid": v(11.18, 8527.84) * mm, "end": v(6, 8529.4) * mm});
            skArc(sketch, "E112.0.6.16", {"start": v(6, 8470.6) * mm, "mid": v(11.18, 8472.16) * mm, "end": v(16, 8474.62) * mm});
            skLineSegment(sketch, "E112.0.6.17", {"start": v(16, 8474.62) * mm, "end": v(16, 8525.38) * mm});
            skLineSegment(sketch, "E112.0.6.18", {"start": v(-6, 8508) * mm, "end": v(6, 8508) * mm});
            skLineSegment(sketch, "E112.0.6.19", {"start": v(-6, 8492) * mm, "end": v(6, 8492) * mm});
            skCircle(sketch, "E112.0.7.0", {"center": v(0, 9700) * mm, "radius": 40 * mm, "construction": true});
            skPoint(sketch, "E112.0.7.1", {"position": v(6, 9730) * mm});
            skPoint(sketch, "E112.0.7.2", {"position": v(6, 9670) * mm});
            skPoint(sketch, "E112.0.7.3", {"position": v(6, 9685) * mm});
            skPoint(sketch, "E112.0.7.4", {"position": v(6, 9700) * mm});
            skPoint(sketch, "E112.0.7.5", {"position": v(6, 9715) * mm});
            skLineSegment(sketch, "E112.0.7.6", {"start": v(-16, 9674.62) * mm, "end": v(-16, 9725.38) * mm});
            skArc(sketch, "E112.0.7.7", {"start": v(-16, 9674.62) * mm, "mid": v(-11.18, 9672.16) * mm, "end": v(-6, 9670.6) * mm});
            skLineSegment(sketch, "E112.0.7.8", {"start": v(-6, 9670.6) * mm, "end": v(19, 9670.6) * mm, "construction": true});
            skArc(sketch, "E112.0.7.9", {"start": v(-6, 9729.4) * mm, "mid": v(-11.18, 9727.84) * mm, "end": v(-16, 9725.38) * mm});
            skLineSegment(sketch, "E112.0.7.10", {"start": v(-6, 9708) * mm, "end": v(-6, 9729.4) * mm});
            skLineSegment(sketch, "E112.0.7.11", {"start": v(-20.78, 9700) * mm, "end": v(22.57, 9700) * mm, "construction": true});
            skLineSegment(sketch, "E112.0.7.12", {"start": v(6, 9708) * mm, "end": v(6, 9729.4) * mm});
            skLineSegment(sketch, "E112.0.7.13", {"start": v(-6, 9692) * mm, "end": v(-6, 9670.6) * mm});
            skLineSegment(sketch, "E112.0.7.14", {"start": v(6, 9692) * mm, "end": v(6, 9670.6) * mm});
            skArc(sketch, "E112.0.7.15", {"start": v(16, 9725.38) * mm, "mid": v(11.18, 9727.84) * mm, "end": v(6, 9729.4) * mm});
            skArc(sketch, "E112.0.7.16", {"start": v(6, 9670.6) * mm, "mid": v(11.18, 9672.16) * mm, "end": v(16, 9674.62) * mm});
            skLineSegment(sketch, "E112.0.7.17", {"start": v(16, 9674.62) * mm, "end": v(16, 9725.38) * mm});
            skLineSegment(sketch, "E112.0.7.18", {"start": v(-6, 9708) * mm, "end": v(6, 9708) * mm});
            skLineSegment(sketch, "E112.0.7.19", {"start": v(-6, 9692) * mm, "end": v(6, 9692) * mm});
            skLineSegment(sketch, "E112.direction1", {"start": v(-16, 1274.62) * mm, "end": v(9, 1274.62) * mm, "construction": true});
            skLineSegment(sketch, "E112.direction2", {"start": v(-16, 1274.62) * mm, "end": v(-16, 2474.62) * mm, "construction": true});
            skSolve(sketch);
        }
        {
            var Q0;
            Q0 = qSketchRegion(id + "F25", true);
            extrude(context, id + "F26", {"entities" : qUnion([Q0]), "depth" : 800 * mm, "offsetDistance" : 25 * mm});
        }
        {
            var Q0;
            Q0=makeQuery(id+"F26.opExtrude","SWEPT_FACE",FACE,{"disambiguationData":[OSD([sQuery(id+"F25.wireOp",EDGE,"E112.0.7.18")])]});
            var sketch = newSketch(context, id + "F27", { "sketchPlane" : qUnion([Q0])});
            skLineSegment(sketch, "E113", {"start": v(-6, -1472.32) * mm, "end": v(6, -1472.32) * mm, "construction": true});
            skArc(sketch, "E114", {"start": v(-6, -1443.33) * mm, "mid": v(-11.33, -1445.6) * mm, "end": v(-16, -1449.02) * mm});
            skLineSegment(sketch, "E115", {"start": v(-6, -1443.33) * mm, "end": v(-6, -1457.32) * mm});
            skLineSegment(sketch, "E116", {"start": v(-6, -1457.32) * mm, "end": v(6, -1457.32) * mm});
            skLineSegment(sketch, "E117", {"start": v(6, -1457.32) * mm, "end": v(6, -1442.82) * mm});
            skLineSegment(sketch, "E118.0", {"start": v(-16, -1449.02) * mm, "end": v(-16, -1473.75) * mm});
            skLineSegment(sketch, "E118.1", {"start": v(16, -1447.3) * mm, "end": v(16, -1473.75) * mm});
            skPoint(sketch, "E119.orphan", {"position": v(-16, -673.75) * mm});
            skPoint(sketch, "E120.orphan", {"position": v(16, -673.75) * mm});
            skArc(sketch, "E121.trimOffspring", {"start": v(16, -1447.3) * mm, "mid": v(11.25, -1444.5) * mm, "end": v(6, -1442.82) * mm});
            skPoint(sketch, "E122.orphan", {"position": v(16, -1473.75) * mm});
            skLineSegment(sketch, "E123", {"start": v(-16, -1473.75) * mm, "end": v(16, -1473.75) * mm});
            skSolve(sketch);
        }
        {
            var Q0;
            Q0 = qSketchRegion(id + "F27", true);
            var Q1;
            Q1=makeQuery(id+"F26.opExtrude","SWEPT_FACE",FACE,{"disambiguationData":[OSD([sQuery(id+"F25.wireOp",EDGE,"E88")])]});
            extrude(context, id + "F28", {"entities" : qUnion([Q0]), "operationType" : NewBodyOperationType.ADD, "endBound" : BoundingType.UP_TO_SURFACE, "oppositeDirection" : true, "depth" : 25 * mm, "endBoundEntityFace" : qUnion([Q1]), "offsetDistance" : 25 * mm});
        }
        {
            var Q0;
            Q0=makeQuery(id+"F26.opExtrude","CAP_FACE",FACE,{"disambiguationData":[OSD([sQuery(id+"F25.wireOp",EDGE,"E84"),sQuery(id+"F25.wireOp",EDGE,"E86.0"),sQuery(id+"F25.wireOp",EDGE,"E87.0"),sQuery(id+"F25.wireOp",EDGE,"E88"),sQuery(id+"F25.wireOp",EDGE,"E108"),sQuery(id+"F25.wireOp",EDGE,"E109"),sQuery(id+"F25.wireOp",EDGE,"E110.trimOffspring"),sQuery(id+"F25.wireOp",EDGE,"E111.trimOffspring")])],"isStart":false});
            var sketch = newSketch(context, id + "F29", { "sketchPlane" : qUnion([Q0])});
            skLineSegment(sketch, "E124", {"start": v(-16, 74.62) * mm, "end": v(-16, 9725.6) * mm});
            skLineSegment(sketch, "E125", {"start": v(-16, 9725.6) * mm, "end": v(-16, 9785.6) * mm});
            skLineSegment(sketch, "E126", {"start": v(-16, 9785.6) * mm, "end": v(-66, 9785.6) * mm});
            skLineSegment(sketch, "E127", {"start": v(-66, 9785.6) * mm, "end": v(-66, 74.62) * mm});
            skLineSegment(sketch, "E128", {"start": v(-66, 74.62) * mm, "end": v(-66, 14.62) * mm});
            skLineSegment(sketch, "E129", {"start": v(-66, 14.62) * mm, "end": v(-16, 14.62) * mm});
            skLineSegment(sketch, "E130", {"start": v(-16, 14.62) * mm, "end": v(-16, 74.62) * mm});
            skLineSegment(sketch, "E131", {"start": v(0, 70) * mm, "end": v(0, 100) * mm, "construction": true});
            skLineSegment(sketch, "E132.MirrorCS", {"start": v(66, 14.62) * mm, "end": v(16, 14.62) * mm});
            skLineSegment(sketch, "E133.MirrorCS", {"start": v(16, 14.62) * mm, "end": v(16, 74.62) * mm});
            skLineSegment(sketch, "E134.MirrorCS", {"start": v(66, 74.62) * mm, "end": v(66, 14.62) * mm});
            skLineSegment(sketch, "E135.MirrorCS", {"start": v(16, 9725.6) * mm, "end": v(16, 9785.6) * mm});
            skLineSegment(sketch, "E136.MirrorCS", {"start": v(16, 9785.6) * mm, "end": v(66, 9785.6) * mm});
            skLineSegment(sketch, "E137.MirrorCS", {"start": v(66, 9785.6) * mm, "end": v(66, 74.62) * mm});
            skLineSegment(sketch, "E138.MirrorCS", {"start": v(16, 74.62) * mm, "end": v(16, 9725.6) * mm});
            skLineSegment(sketch, "E139", {"start": v(66, -45.38) * mm, "end": v(-126, -45.38) * mm});
            skLineSegment(sketch, "E140", {"start": v(66, -45.38) * mm, "end": v(126, -45.38) * mm});
            skLineSegment(sketch, "E141", {"start": v(126, -45.38) * mm, "end": v(126, 9785.6) * mm});
            skLineSegment(sketch, "E142", {"start": v(126, 9785.6) * mm, "end": v(126, 9845.6) * mm});
            skLineSegment(sketch, "E143", {"start": v(126, 9845.6) * mm, "end": v(-66, 9845.6) * mm});
            skLineSegment(sketch, "E144", {"start": v(-66, 9845.6) * mm, "end": v(-126, 9845.6) * mm});
            skLineSegment(sketch, "E145", {"start": v(-126, 9845.6) * mm, "end": v(-126, -45.38) * mm});
            skSolve(sketch);
        }
        {
            var Q0;
            Q0 = qSketchRegion(id + "F29", true);
            extrude(context, id + "F30", {"entities" : qUnion([Q0]), "operationType" : NewBodyOperationType.ADD, "depth" : 50 * mm, "offsetDistance" : 25 * mm});
        }
        {
            var Q0;
            Q0=makeQuery(id+"F30.opExtrude","SWEPT_EDGE",EDGE,{"disambiguationData":[OSD([sQuery(id+"F29.wireOp",EDGE,"E140"),sQuery(id+"F29.wireOp",EDGE,"E141")])]});
            var Q1;
            Q1=makeQuery(id+"F30.opExtrude","SWEPT_EDGE",EDGE,{"disambiguationData":[OSD([sQuery(id+"F29.wireOp",EDGE,"E139"),sQuery(id+"F29.wireOp",EDGE,"E145")])]});
            var Q2;
            Q2=makeQuery(id+"F30.opExtrude","SWEPT_EDGE",EDGE,{"disambiguationData":[OSD([sQuery(id+"F29.wireOp",EDGE,"E142"),sQuery(id+"F29.wireOp",EDGE,"E143")])]});
            var Q3;
            Q3=makeQuery(id+"F30.opExtrude","SWEPT_EDGE",EDGE,{"disambiguationData":[OSD([sQuery(id+"F29.wireOp",EDGE,"E144"),sQuery(id+"F29.wireOp",EDGE,"E145")])]});
            fillet(context, id + "F31", {"entities" : qUnion([Q0, Q1, Q2, Q3]), "radius" : 20 * mm, "tangentPropagation" : true, "allowEdgeOverflow" : false});
        }
        {
            var Q0;
            Q0=makeQuery(id+"F30.opExtrude","SWEPT_EDGE",EDGE,{"disambiguationData":[OSD([sQuery(id+"F29.wireOp",EDGE,"E126"),sQuery(id+"F29.wireOp",EDGE,"E127")])]});
            var Q1;
            Q1=makeQuery(id+"F30.opExtrude","SWEPT_EDGE",EDGE,{"disambiguationData":[OSD([sQuery(id+"F29.wireOp",EDGE,"E125"),sQuery(id+"F29.wireOp",EDGE,"E126")])]});
            var Q2;
            Q2=makeQuery(id+"F30.opExtrude","SWEPT_EDGE",EDGE,{"disambiguationData":[OSD([sQuery(id+"F29.wireOp",EDGE,"E135.MirrorCS"),sQuery(id+"F29.wireOp",EDGE,"E136.MirrorCS")])]});
            var Q3;
            Q3=makeQuery(id+"F30.opExtrude","SWEPT_EDGE",EDGE,{"disambiguationData":[OSD([sQuery(id+"F29.wireOp",EDGE,"E136.MirrorCS"),sQuery(id+"F29.wireOp",EDGE,"E137.MirrorCS")])]});
            var Q4;
            Q4=makeQuery(id+"F30.opExtrude","SWEPT_EDGE",EDGE,{"disambiguationData":[OSD([sQuery(id+"F29.wireOp",EDGE,"E132.MirrorCS"),sQuery(id+"F29.wireOp",EDGE,"E134.MirrorCS")])]});
            var Q5;
            Q5=makeQuery(id+"F30.opExtrude","SWEPT_EDGE",EDGE,{"disambiguationData":[OSD([sQuery(id+"F29.wireOp",EDGE,"E132.MirrorCS"),sQuery(id+"F29.wireOp",EDGE,"E133.MirrorCS")])]});
            var Q6;
            Q6=makeQuery(id+"F30.opExtrude","SWEPT_EDGE",EDGE,{"disambiguationData":[OSD([sQuery(id+"F29.wireOp",EDGE,"E129"),sQuery(id+"F29.wireOp",EDGE,"E130")])]});
            var Q7;
            Q7=makeQuery(id+"F30.opExtrude","SWEPT_EDGE",EDGE,{"disambiguationData":[OSD([sQuery(id+"F29.wireOp",EDGE,"E128"),sQuery(id+"F29.wireOp",EDGE,"E129")])]});
            fillet(context, id + "F32", {"entities" : qUnion([Q0, Q1, Q2, Q3, Q4, Q5, Q6, Q7]), "radius" : 10 * mm, "tangentPropagation" : true, "allowEdgeOverflow" : false});
        }
        {
            var Q0;
            Q0=makeQuery(id+"F30.opExtrude","CAP_EDGE",EDGE,{"disambiguationData":[OSD([sQuery(id+"F29.wireOp",EDGE,"E141"),sQuery(id+"F29.wireOp",EDGE,"E142")])],"isStart":false});
            var Q1;
            Q1=makeQuery(id+"F30.opExtrude","CAP_EDGE",EDGE,{"disambiguationData":[OSD([sQuery(id+"F29.wireOp",EDGE,"E141"),sQuery(id+"F29.wireOp",EDGE,"E142")])],"isStart":true});
            var Q2;
            Q2=makeQuery(id+"F30.opExtrude","CAP_EDGE",EDGE,{"disambiguationData":[OSD([sQuery(id+"F29.wireOp",EDGE,"E133.MirrorCS"),sQuery(id+"F29.wireOp",EDGE,"E135.MirrorCS"),sQuery(id+"F29.wireOp",EDGE,"E138.MirrorCS")])],"isStart":false});
            var Q3;
            Q3=makeQuery(id+"F30.opExtrude","CAP_EDGE",EDGE,{"disambiguationData":[OSD([sQuery(id+"F29.wireOp",EDGE,"E124"),sQuery(id+"F29.wireOp",EDGE,"E125"),sQuery(id+"F29.wireOp",EDGE,"E130")])],"isStart":false});
            fillet(context, id + "F33", {"entities" : qUnion([Q0, Q1, Q2, Q3]), "radius" : 10 * mm, "tangentPropagation" : true, "allowEdgeOverflow" : false});
        }
        {
            var Q0;
            Q0=makeQuery(id+"F28.boolean.opBoolean","MERGE",FACE,{"derivedFrom":[makeQuery(id+"F26.opExtrude","SWEPT_FACE",FACE,{"disambiguationData":[OSD([sQuery(id+"F25.wireOp",EDGE,"E112.0.6.10")])]}),makeQuery(id+"F26.opExtrude","SWEPT_FACE",FACE,{"disambiguationData":[OSD([sQuery(id+"F25.wireOp",EDGE,"E112.0.7.13")])]}),makeQuery(id+"F28.opExtrude","SWEPT_FACE",FACE,{"disambiguationData":[OSD([sQuery(id+"F27.wireOp",EDGE,"E117")])]})]});
            var sketch = newSketch(context, id + "F34", { "sketchPlane" : qUnion([Q0])});
            skLineSegment(sketch, "E146.0", {"start": v(9692, -673.75) * mm, "end": v(9692, -1457.32) * mm});
            skLineSegment(sketch, "E146.1", {"start": v(8508, -1457.32) * mm, "end": v(9692, -1457.32) * mm});
            skLineSegment(sketch, "E146.2", {"start": v(8508, -673.75) * mm, "end": v(8508, -1457.32) * mm});
            skLineSegment(sketch, "E146.3", {"start": v(7308, -1457.32) * mm, "end": v(8492, -1457.32) * mm});
            skLineSegment(sketch, "E146.4", {"start": v(8492, -673.75) * mm, "end": v(8492, -1457.32) * mm});
            skLineSegment(sketch, "E146.5", {"start": v(7308, -673.75) * mm, "end": v(7308, -1457.32) * mm});
            skLineSegment(sketch, "E146.6", {"start": v(6108, -1457.32) * mm, "end": v(7292, -1457.32) * mm});
            skLineSegment(sketch, "E146.7", {"start": v(7292, -673.75) * mm, "end": v(7292, -1457.32) * mm});
            skLineSegment(sketch, "E146.8", {"start": v(6108, -673.75) * mm, "end": v(6108, -1457.32) * mm});
            skLineSegment(sketch, "E146.9", {"start": v(4908, -1457.32) * mm, "end": v(6092, -1457.32) * mm});
            skLineSegment(sketch, "E146.10", {"start": v(6092, -673.75) * mm, "end": v(6092, -1457.32) * mm});
            skLineSegment(sketch, "E146.11", {"start": v(4908, -673.75) * mm, "end": v(4908, -1457.32) * mm});
            skLineSegment(sketch, "E146.12", {"start": v(4892, -673.75) * mm, "end": v(4892, -1457.32) * mm});
            skLineSegment(sketch, "E146.13", {"start": v(3708, -1457.32) * mm, "end": v(4892, -1457.32) * mm});
            skLineSegment(sketch, "E146.14", {"start": v(3708, -673.75) * mm, "end": v(3708, -1457.32) * mm});
            skLineSegment(sketch, "E146.15", {"start": v(2508, -1457.32) * mm, "end": v(3692, -1457.32) * mm});
            skLineSegment(sketch, "E146.16", {"start": v(3692, -673.75) * mm, "end": v(3692, -1457.32) * mm});
            skLineSegment(sketch, "E146.17", {"start": v(2508, -673.75) * mm, "end": v(2508, -1457.32) * mm});
            skLineSegment(sketch, "E146.18", {"start": v(1308, -1457.32) * mm, "end": v(2492, -1457.32) * mm});
            skLineSegment(sketch, "E146.19", {"start": v(2492, -673.75) * mm, "end": v(2492, -1457.32) * mm});
            skLineSegment(sketch, "E146.20", {"start": v(1308, -673.75) * mm, "end": v(1308, -1457.32) * mm});
            skLineSegment(sketch, "E146.21", {"start": v(100, -1457.32) * mm, "end": v(1292, -1457.32) * mm});
            skLineSegment(sketch, "E146.22", {"start": v(1292, -673.75) * mm, "end": v(1292, -1457.32) * mm});
            skLineSegment(sketch, "E146.23", {"start": v(100, -673.75) * mm, "end": v(100, -1457.32) * mm});
            skLineSegment(sketch, "E147", {"start": v(100, -673.75) * mm, "end": v(1292, -673.75) * mm});
            skLineSegment(sketch, "E148", {"start": v(1308, -673.75) * mm, "end": v(2492, -673.75) * mm});
            skLineSegment(sketch, "E149", {"start": v(2508, -673.75) * mm, "end": v(3692, -673.75) * mm});
            skLineSegment(sketch, "E150", {"start": v(3708, -673.75) * mm, "end": v(4892, -673.75) * mm});
            skLineSegment(sketch, "E151", {"start": v(4908, -673.75) * mm, "end": v(6092, -673.75) * mm});
            skLineSegment(sketch, "E152", {"start": v(6108, -673.75) * mm, "end": v(7292, -673.75) * mm});
            skLineSegment(sketch, "E153", {"start": v(7308, -673.75) * mm, "end": v(8492, -673.75) * mm});
            skLineSegment(sketch, "E154", {"start": v(8508, -673.75) * mm, "end": v(9692, -673.75) * mm});
            skSolve(sketch);
        }
        {
            var Q0;
            Q0 = qSketchRegion(id + "F34", true);
            var Q1;
            Q1=makeQuery(id+"F28.boolean.opBoolean","MERGE",FACE,{"derivedFrom":[makeQuery(id+"F26.opExtrude","SWEPT_FACE",FACE,{"disambiguationData":[OSD([sQuery(id+"F25.wireOp",EDGE,"E112.0.6.12")])]}),makeQuery(id+"F26.opExtrude","SWEPT_FACE",FACE,{"disambiguationData":[OSD([sQuery(id+"F25.wireOp",EDGE,"E112.0.7.14")])]}),makeQuery(id+"F28.opExtrude","SWEPT_FACE",FACE,{"disambiguationData":[OSD([sQuery(id+"F27.wireOp",EDGE,"E115")])]})]});
            extrude(context, id + "F35", {"entities" : qUnion([Q0]), "endBound" : BoundingType.UP_TO_SURFACE, "depth" : 25 * mm, "endBoundEntityFace" : qUnion([Q1]), "offsetDistance" : 25 * mm});
        }
        {
            var Q0;
            Q0=makeQuery(id+"F6.opSweep","MID_CAP_EDGE",EDGE,{"disambiguationData":[OSD([sQuery(id+"F4.wireOp",EDGE,"E14.1"),sQuery(id+"F5.wireOp",VERTEX,"E18.start")])],"capPos":1.0});
            var Q1;
            Q1=makeQuery(id+"F6.opSweep","MID_CAP_EDGE",EDGE,{"disambiguationData":[OSD([sQuery(id+"F4.wireOp",EDGE,"E14.2"),sQuery(id+"F5.wireOp",VERTEX,"E18.start")])],"capPos":1.0});
            var Q2;
            Q2=makeQuery(id+"F9.opSweep","MID_CAP_EDGE",EDGE,{"disambiguationData":[OSD([sQuery(id+"F7.wireOp",EDGE,"E19.4"),sQuery(id+"F8.wireOp",VERTEX,"E23.start")])],"capPos":1.0});
            var Q3;
            Q3=makeQuery(id+"F9.opSweep","MID_CAP_EDGE",EDGE,{"disambiguationData":[OSD([sQuery(id+"F7.wireOp",EDGE,"E19.0"),sQuery(id+"F8.wireOp",VERTEX,"E23.start")])],"capPos":1.0});
            fillet(context, id + "F36", {"entities" : qUnion([Q0, Q1, Q2, Q3]), "radius" : 10 * mm, "tangentPropagation" : true, "allowEdgeOverflow" : false});
        }
        {
            var Q0;
            Q0=makeQuery(id+"F13.opSweep","CAP_FACE",FACE,{"disambiguationData":[OSD([sQuery(id+"F0.wireOp",EDGE,"E9.0"),sQuery(id+"F0.wireOp",EDGE,"E9.4"),sQuery(id+"F12.wireOp",EDGE,"E30"),sQuery(id+"F12.wireOp",EDGE,"E31"),sQuery(id+"F12.wireOp",EDGE,"E32"),sQuery(id+"F12.wireOp",EDGE,"E33"),sQuery(id+"F12.wireOp",EDGE,"E34"),sQuery(id+"F12.wireOp",EDGE,"E35"),sQuery(id+"F12.wireOp",EDGE,"E36"),sQuery(id+"F12.wireOp",EDGE,"E37"),sQuery(id+"F12.wireOp",EDGE,"E38"),sQuery(id+"F12.wireOp",EDGE,"E39"),sQuery(id+"F12.wireOp",EDGE,"E40"),sQuery(id+"F12.wireOp",EDGE,"E41.trimOffspring"),sQuery(id+"F12.wireOp",EDGE,"E42.trimOffspring"),sQuery(id+"F12.wireOp",EDGE,"E44"),sQuery(id+"F12.wireOp",EDGE,"E45"),sQuery(id+"F12.wireOp",EDGE,"E46.MirrorCS"),sQuery(id+"F12.wireOp",EDGE,"E47.MirrorCS"),sQuery(id+"F12.wireOp",EDGE,"E48.trimOffspring")])],"isStart":true});
            var sketch = newSketch(context, id + "F37", { "sketchPlane" : qUnion([Q0])});
            skLineSegment(sketch, "E155", {"start": v(3024.32, -541.62) * mm, "end": v(3044.32, -541.62) * mm});
            skLineSegment(sketch, "E156", {"start": v(3044.32, -541.62) * mm, "end": v(3044.32, -556.62) * mm});
            skLineSegment(sketch, "E157", {"start": v(3039.32, -561.62) * mm, "end": v(3029.32, -561.62) * mm});
            skLineSegment(sketch, "E158", {"start": v(3024.32, -556.62) * mm, "end": v(3024.32, -541.62) * mm});
            skPoint(sketch, "E159.visualSharp", {"position": v(3024.32, -561.62) * mm});
            skArc(sketch, "E159.filletArc", {"start": v(3024.32, -556.62) * mm, "mid": v(3025.78, -560.16) * mm, "end": v(3029.32, -561.62) * mm});
            skPoint(sketch, "E160.visualSharp", {"position": v(3044.32, -561.62) * mm});
            skArc(sketch, "E160.filletArc", {"start": v(3039.32, -561.62) * mm, "mid": v(3042.85, -560.16) * mm, "end": v(3044.32, -556.62) * mm});
            skSolve(sketch);
        }
        {
            var Q0;
            Q0 = qSketchRegion(id + "F37", true);
            var Q1;
            Q1=makeQuery(id+"F13.opSweep","SWEPT_EDGE",EDGE,{"disambiguationData":[OSD([sQuery(id+"F0.wireOp",EDGE,"E9.0"),sQuery(id+"F0.wireOp",EDGE,"E9.4"),sQuery(id+"F4.wireOp",EDGE,"E14.1"),sQuery(id+"F4.wireOp",EDGE,"E14.2"),sQuery(id+"F5.wireOp",EDGE,"E17"),sQuery(id+"F12.wireOp",EDGE,"E46.MirrorCS"),sQuery(id+"F12.wireOp",EDGE,"E47.MirrorCS")])]});
            var Q2;
            Q2=makeQuery(id+"F13.opSweep","SWEPT_EDGE",EDGE,{"disambiguationData":[OSD([sQuery(id+"F4.wireOp",EDGE,"E14.1"),sQuery(id+"F4.wireOp",EDGE,"E14.2"),sQuery(id+"F5.wireOp",EDGE,"E18"),sQuery(id+"F12.wireOp",EDGE,"E46.MirrorCS"),sQuery(id+"F12.wireOp",EDGE,"E47.MirrorCS")])]});
            sweep(context, id + "F38", {"profiles" : qUnion([Q0]), "path" : qUnion([Q1, Q2])});
        }
        {
            var Q0;
            Q0=makeQuery(id+"F15.opSweep","CAP_FACE",FACE,{"disambiguationData":[OSD([sQuery(id+"F0.wireOp",EDGE,"E9.1"),sQuery(id+"F0.wireOp",EDGE,"E9.2"),sQuery(id+"F14.wireOp",EDGE,"E52.MirrorCS"),sQuery(id+"F14.wireOp",EDGE,"E53.MirrorCS"),sQuery(id+"F14.wireOp",EDGE,"E54.MirrorCS"),sQuery(id+"F14.wireOp",EDGE,"E55.MirrorCS"),sQuery(id+"F14.wireOp",EDGE,"E56.MirrorCS"),sQuery(id+"F14.wireOp",EDGE,"E57.MirrorCS"),sQuery(id+"F14.wireOp",EDGE,"E58.MirrorCS"),sQuery(id+"F14.wireOp",EDGE,"E59.MirrorCS"),sQuery(id+"F14.wireOp",EDGE,"E60.MirrorCS"),sQuery(id+"F14.wireOp",EDGE,"E61.MirrorCS"),sQuery(id+"F14.wireOp",EDGE,"E62.MirrorCS"),sQuery(id+"F14.wireOp",EDGE,"E63.MirrorCS"),sQuery(id+"F14.wireOp",EDGE,"E64.MirrorCS"),sQuery(id+"F14.wireOp",EDGE,"E65.MirrorCS"),sQuery(id+"F14.wireOp",EDGE,"E66.MirrorCS"),sQuery(id+"F14.wireOp",EDGE,"E67.MirrorCS"),sQuery(id+"F14.wireOp",EDGE,"E68.MirrorCS"),sQuery(id+"F14.wireOp",EDGE,"E69.MirrorCS")])],"isStart":true});
            var sketch = newSketch(context, id + "F39", { "sketchPlane" : qUnion([Q0])});
            skLineSegment(sketch, "E161", {"start": v(-3044.32, -541.62) * mm, "end": v(-3044.32, -556.62) * mm});
            skLineSegment(sketch, "E162", {"start": v(-3039.32, -561.62) * mm, "end": v(-3029.32, -561.62) * mm});
            skLineSegment(sketch, "E163", {"start": v(-3024.32, -556.62) * mm, "end": v(-3024.32, -541.62) * mm});
            skLineSegment(sketch, "E164", {"start": v(-3024.32, -541.62) * mm, "end": v(-3044.32, -541.62) * mm});
            skPoint(sketch, "E165.visualSharp", {"position": v(-3044.32, -561.62) * mm});
            skArc(sketch, "E165.filletArc", {"start": v(-3044.32, -556.62) * mm, "mid": v(-3042.85, -560.16) * mm, "end": v(-3039.32, -561.62) * mm});
            skPoint(sketch, "E166.visualSharp", {"position": v(-3024.32, -561.62) * mm});
            skArc(sketch, "E166.filletArc", {"start": v(-3029.32, -561.62) * mm, "mid": v(-3025.78, -560.16) * mm, "end": v(-3024.32, -556.62) * mm});
            skSolve(sketch);
        }
        {
            var Q0;
            Q0 = qSketchRegion(id + "F39", true);
            var Q1;
            Q1=makeQuery(id+"F15.opSweep","SWEPT_EDGE",EDGE,{"disambiguationData":[OSD([sQuery(id+"F0.wireOp",EDGE,"E9.1"),sQuery(id+"F0.wireOp",EDGE,"E9.2"),sQuery(id+"F7.wireOp",EDGE,"E19.0"),sQuery(id+"F7.wireOp",EDGE,"E19.4"),sQuery(id+"F8.wireOp",EDGE,"E22"),sQuery(id+"F14.wireOp",EDGE,"E58.MirrorCS"),sQuery(id+"F14.wireOp",EDGE,"E69.MirrorCS")])]});
            var Q2;
            Q2=makeQuery(id+"F15.opSweep","SWEPT_EDGE",EDGE,{"disambiguationData":[OSD([sQuery(id+"F7.wireOp",EDGE,"E19.0"),sQuery(id+"F7.wireOp",EDGE,"E19.4"),sQuery(id+"F8.wireOp",EDGE,"E23"),sQuery(id+"F14.wireOp",EDGE,"E58.MirrorCS"),sQuery(id+"F14.wireOp",EDGE,"E69.MirrorCS")])]});
            sweep(context, id + "F40", {"profiles" : qUnion([Q0]), "path" : qUnion([Q1, Q2])});
        }
    });
